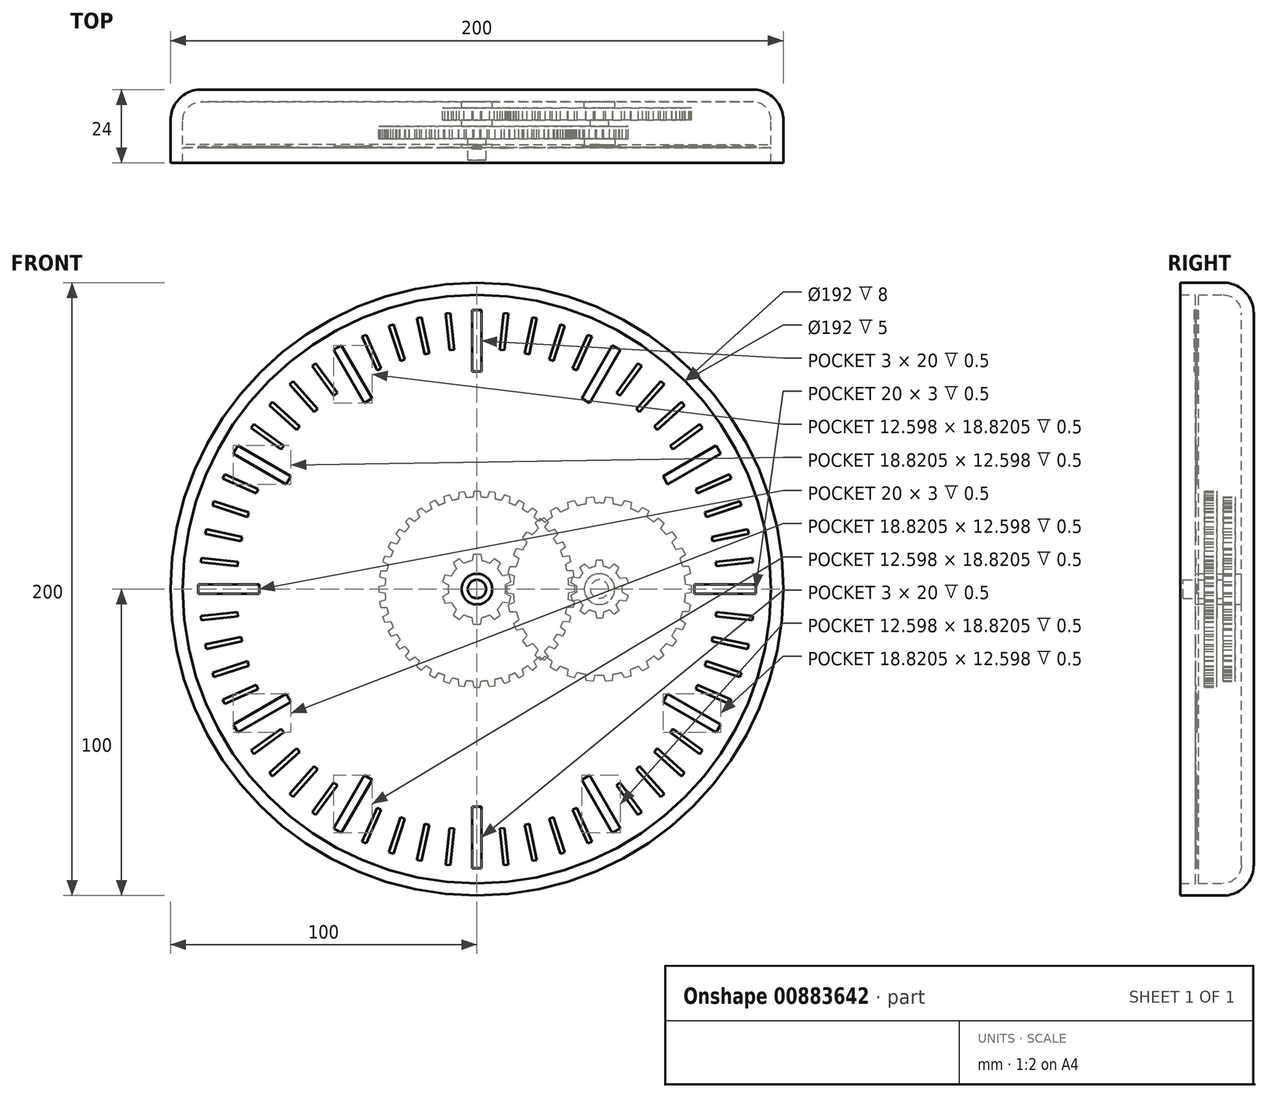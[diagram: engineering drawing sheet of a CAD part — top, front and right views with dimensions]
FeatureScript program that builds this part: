
annotation { "Feature Type Name" : "Feature", "Feature Type Description" : "" }
export const myFeature = defineFeature(function(context is Context, id is Id, definition is map)
    precondition{}
    {
        {
            var Q0;
            Q0=qCreatedBy(makeId("Front.planeOp"),FACE);
            var sketch = newSketch(context, id + "F0", { "sketchPlane" : qUnion([Q0])});
            skCircle(sketch, "E0", {"center": v(0, 0) * mm, "radius": 100 * mm});
            skSolve(sketch);
        }
        {
            var Q0;
            Q0 = qSketchRegion(id + "F0", true);
            extrude(context, id + "F1", {"entities" : qUnion([Q0]), "depth" : 24 * mm, "offsetDistance" : 25 * mm});
        }
        {
            var Q0;
            Q0=makeQuery(id+"F1.opExtrude","CAP_EDGE",EDGE,{"disambiguationData":[OSD([sQuery(id+"F0.wireOp",EDGE,"E0")])],"isStart":true});
            fillet(context, id + "F2", {"entities" : qUnion([Q0]), "radius" : 10 * mm, "tangentPropagation" : true, "allowEdgeOverflow" : false});
        }
        {
            var Q0;
            Q0=makeQuery(id+"F1.opExtrude","CAP_FACE",FACE,{"disambiguationData":[OSD([sQuery(id+"F0.wireOp",EDGE,"E0")])],"isStart":false});
            shell(context, id + "F3", {"entities" : qUnion([Q0]), "thickness" : 4 * mm});
        }
        {
            var Q0;
            {var subQ0=sQuery(id+"F0.wireOp",EDGE,"E0");Q0=makeQuery(id+"F3.opShell","OFFSET_FACE",FACE,{"disambiguationData":[OSD([subQ0]),TDD([makeQuery(id+"F1.opExtrude","CAP_FACE",FACE,{"disambiguationData":[OSD([subQ0])],"isStart":true})])]});}
            var sketch = newSketch(context, id + "F4", { "sketchPlane" : qUnion([Q0])});
            skCircle(sketch, "E1", {"center": v(0, 0) * mm, "radius": 3 * mm});
            skCircle(sketch, "E2", {"center": v(0, 0) * mm, "radius": 5 * mm});
            skCircle(sketch, "E3", {"center": v(40, 0) * mm, "radius": 3 * mm});
            skCircle(sketch, "E4", {"center": v(40, 0) * mm, "radius": 5 * mm});
            skSolve(sketch);
        }
        {
            var Q0;
            Q0 = qSketchRegion(id + "F4", true);
            extrude(context, id + "F5", {"entities" : qUnion([Q0]), "operationType" : NewBodyOperationType.ADD, "depth" : 2 * mm, "offsetDistance" : 25 * mm});
        }
        {
            var Q0;
            {var subQ0=sQuery(id+"F0.wireOp",EDGE,"E0");Q0=makeQuery(id+"F5.boolean.opBoolean","SPLIT",FACE,{"disambiguationData":[TD([makeQuery(id+"F5.opExtrude","SWEPT_FACE",FACE,{"disambiguationData":[OSD([sQuery(id+"F4.wireOp",EDGE,"E1")])]})])],"derivedFrom":makeQuery(id+"F3.opShell","OFFSET_FACE",FACE,{"disambiguationData":[OSD([subQ0]),TDD([makeQuery(id+"F1.opExtrude","CAP_FACE",FACE,{"disambiguationData":[OSD([subQ0])],"isStart":true})])]})});}
            extrude(context, id + "F6", {"entities" : qUnion([Q0]), "depth" : 19 * mm, "offsetDistance" : 25 * mm});
        }
        {
            var Q0;
            {var subQ0=sQuery(id+"F0.wireOp",EDGE,"E0");Q0=makeQuery(id+"F5.boolean.opBoolean","SPLIT",FACE,{"disambiguationData":[TD([makeQuery(id+"F5.opExtrude","SWEPT_FACE",FACE,{"disambiguationData":[OSD([sQuery(id+"F4.wireOp",EDGE,"E3")])]})])],"derivedFrom":makeQuery(id+"F3.opShell","OFFSET_FACE",FACE,{"disambiguationData":[OSD([subQ0]),TDD([makeQuery(id+"F1.opExtrude","CAP_FACE",FACE,{"disambiguationData":[OSD([subQ0])],"isStart":true})])]})});}
            extrude(context, id + "F7", {"entities" : qUnion([Q0]), "depth" : 8 * mm, "offsetDistance" : 25 * mm});
        }
        {
            var Q0;
            Q0=makeQuery(id+"F5.opExtrude","CAP_FACE",FACE,{"disambiguationData":[OSD([sQuery(id+"F4.wireOp",EDGE,"E1"),sQuery(id+"F4.wireOp",EDGE,"E2")])],"isStart":false});
            var sketch = newSketch(context, id + "F8", { "sketchPlane" : qUnion([Q0])});
            skCircle(sketch, "E5", {"center": v(0, 0) * mm, "radius": 9.38 * mm});
            skLineSegment(sketch, "E6", {"start": v(0, 11.38) * mm, "end": v(1.18, 11.38) * mm});
            skLineSegment(sketch, "E7", {"start": v(1.18, 11.38) * mm, "end": v(1.55, 9.25) * mm});
            skLineSegment(sketch, "E8.MirrorCS", {"start": v(0, 11.38) * mm, "end": v(-1.18, 11.38) * mm});
            skLineSegment(sketch, "E9.MirrorCS", {"start": v(-1.18, 11.38) * mm, "end": v(-1.55, 9.25) * mm});
            skLineSegment(sketch, "E10.1.0", {"start": v(-7.64, 8.51) * mm, "end": v(-6.7, 6.57) * mm});
            skLineSegment(sketch, "E10.1.1", {"start": v(-6.69, 9.2) * mm, "end": v(-7.64, 8.51) * mm});
            skLineSegment(sketch, "E10.1.2", {"start": v(-6.69, 9.2) * mm, "end": v(-5.73, 9.9) * mm});
            skLineSegment(sketch, "E10.1.3", {"start": v(-5.73, 9.9) * mm, "end": v(-4.18, 8.4) * mm});
            skLineSegment(sketch, "E10.2.0", {"start": v(-11.18, 2.4) * mm, "end": v(-9.27, 1.38) * mm});
            skLineSegment(sketch, "E10.2.1", {"start": v(-10.82, 3.52) * mm, "end": v(-11.18, 2.4) * mm});
            skLineSegment(sketch, "E10.2.2", {"start": v(-10.82, 3.52) * mm, "end": v(-10.45, 4.64) * mm});
            skLineSegment(sketch, "E10.2.3", {"start": v(-10.45, 4.64) * mm, "end": v(-8.31, 4.33) * mm});
            skLineSegment(sketch, "E10.3.0", {"start": v(-10.45, -4.64) * mm, "end": v(-8.31, -4.33) * mm});
            skLineSegment(sketch, "E10.3.1", {"start": v(-10.82, -3.52) * mm, "end": v(-10.45, -4.64) * mm});
            skLineSegment(sketch, "E10.3.2", {"start": v(-10.82, -3.52) * mm, "end": v(-11.18, -2.4) * mm});
            skLineSegment(sketch, "E10.3.3", {"start": v(-11.18, -2.4) * mm, "end": v(-9.27, -1.38) * mm});
            skLineSegment(sketch, "E10.4.0", {"start": v(-5.73, -9.9) * mm, "end": v(-4.18, -8.4) * mm});
            skLineSegment(sketch, "E10.4.1", {"start": v(-6.69, -9.2) * mm, "end": v(-5.73, -9.9) * mm});
            skLineSegment(sketch, "E10.4.2", {"start": v(-6.69, -9.2) * mm, "end": v(-7.64, -8.51) * mm});
            skLineSegment(sketch, "E10.4.3", {"start": v(-7.64, -8.51) * mm, "end": v(-6.7, -6.57) * mm});
            skLineSegment(sketch, "E10.5.0", {"start": v(1.18, -11.38) * mm, "end": v(1.55, -9.25) * mm});
            skLineSegment(sketch, "E10.5.1", {"start": v(0, -11.38) * mm, "end": v(1.18, -11.38) * mm});
            skLineSegment(sketch, "E10.5.2", {"start": v(0, -11.38) * mm, "end": v(-1.18, -11.38) * mm});
            skLineSegment(sketch, "E10.5.3", {"start": v(-1.18, -11.38) * mm, "end": v(-1.55, -9.25) * mm});
            skLineSegment(sketch, "E10.6.0", {"start": v(7.64, -8.51) * mm, "end": v(6.7, -6.57) * mm});
            skLineSegment(sketch, "E10.6.1", {"start": v(6.69, -9.2) * mm, "end": v(7.64, -8.51) * mm});
            skLineSegment(sketch, "E10.6.2", {"start": v(6.69, -9.2) * mm, "end": v(5.73, -9.9) * mm});
            skLineSegment(sketch, "E10.6.3", {"start": v(5.73, -9.9) * mm, "end": v(4.18, -8.4) * mm});
            skLineSegment(sketch, "E10.7.0", {"start": v(11.18, -2.4) * mm, "end": v(9.27, -1.38) * mm});
            skLineSegment(sketch, "E10.7.1", {"start": v(10.82, -3.52) * mm, "end": v(11.18, -2.4) * mm});
            skLineSegment(sketch, "E10.7.2", {"start": v(10.82, -3.52) * mm, "end": v(10.45, -4.64) * mm});
            skLineSegment(sketch, "E10.7.3", {"start": v(10.45, -4.64) * mm, "end": v(8.31, -4.33) * mm});
            skLineSegment(sketch, "E10.8.0", {"start": v(10.45, 4.64) * mm, "end": v(8.31, 4.33) * mm});
            skLineSegment(sketch, "E10.8.1", {"start": v(10.82, 3.52) * mm, "end": v(10.45, 4.64) * mm});
            skLineSegment(sketch, "E10.8.2", {"start": v(10.82, 3.52) * mm, "end": v(11.18, 2.4) * mm});
            skLineSegment(sketch, "E10.8.3", {"start": v(11.18, 2.4) * mm, "end": v(9.27, 1.38) * mm});
            skLineSegment(sketch, "E10.9.0", {"start": v(5.73, 9.9) * mm, "end": v(4.18, 8.4) * mm});
            skLineSegment(sketch, "E10.9.1", {"start": v(6.69, 9.2) * mm, "end": v(5.73, 9.9) * mm});
            skLineSegment(sketch, "E10.9.2", {"start": v(6.69, 9.2) * mm, "end": v(7.64, 8.51) * mm});
            skLineSegment(sketch, "E10.9.3", {"start": v(7.64, 8.51) * mm, "end": v(6.7, 6.57) * mm});
            skSolve(sketch);
        }
        {
            var Q0;
            Q0 = qSketchRegion(id + "F8", true);
            extrude(context, id + "F9", {"entities" : qUnion([Q0]), "operationType" : NewBodyOperationType.ADD, "depth" : 4 * mm, "offsetDistance" : 25 * mm});
        }
        {
            var Q0;
            Q0=makeQuery(id+"F5.opExtrude","CAP_FACE",FACE,{"disambiguationData":[OSD([sQuery(id+"F4.wireOp",EDGE,"E3"),sQuery(id+"F4.wireOp",EDGE,"E4")])],"isStart":false});
            var sketch = newSketch(context, id + "F10", { "sketchPlane" : qUnion([Q0])});
            skCircle(sketch, "E11", {"center": v(40, 0) * mm, "radius": 28.12 * mm});
            skLineSegment(sketch, "E12", {"start": v(9.88, 0) * mm, "end": v(9.88, 1.18) * mm});
            skLineSegment(sketch, "E13", {"start": v(9.88, 1.18) * mm, "end": v(11.92, 1.54) * mm});
            skLineSegment(sketch, "E14.MirrorCS", {"start": v(9.88, 0) * mm, "end": v(9.88, -1.18) * mm});
            skLineSegment(sketch, "E15.MirrorCS", {"start": v(9.88, -1.18) * mm, "end": v(11.92, -1.54) * mm});
            skLineSegment(sketch, "E16.1.0", {"start": v(10.29, -5.11) * mm, "end": v(12.21, -4.33) * mm});
            skLineSegment(sketch, "E16.1.1", {"start": v(10.53, -6.26) * mm, "end": v(10.29, -5.11) * mm});
            skLineSegment(sketch, "E16.1.2", {"start": v(10.53, -6.26) * mm, "end": v(10.78, -7.42) * mm});
            skLineSegment(sketch, "E16.1.3", {"start": v(10.78, -7.42) * mm, "end": v(12.85, -7.34) * mm});
            skLineSegment(sketch, "E16.2.0", {"start": v(12, -11.18) * mm, "end": v(13.72, -10.02) * mm});
            skLineSegment(sketch, "E16.2.1", {"start": v(12.48, -12.25) * mm, "end": v(12, -11.18) * mm});
            skLineSegment(sketch, "E16.2.2", {"start": v(12.48, -12.25) * mm, "end": v(12.96, -13.33) * mm});
            skLineSegment(sketch, "E16.2.3", {"start": v(12.96, -13.33) * mm, "end": v(14.97, -12.83) * mm});
            skLineSegment(sketch, "E17.1.3.0", {"start": v(14.94, -16.75) * mm, "end": v(16.38, -15.26) * mm});
            skLineSegment(sketch, "E17.3.3.0", {"start": v(15.63, -17.7) * mm, "end": v(14.94, -16.75) * mm});
            skLineSegment(sketch, "E17.6.3.0", {"start": v(15.63, -17.7) * mm, "end": v(16.32, -18.66) * mm});
            skLineSegment(sketch, "E17.9.3.0", {"start": v(16.32, -18.66) * mm, "end": v(18.18, -17.75) * mm});
            skLineSegment(sketch, "E17.1.4.0", {"start": v(18.97, -21.6) * mm, "end": v(20.07, -19.84) * mm});
            skLineSegment(sketch, "E17.3.4.0", {"start": v(19.84, -22.39) * mm, "end": v(18.97, -21.6) * mm});
            skLineSegment(sketch, "E17.6.4.0", {"start": v(19.84, -22.39) * mm, "end": v(20.72, -23.18) * mm});
            skLineSegment(sketch, "E17.9.4.0", {"start": v(20.72, -23.18) * mm, "end": v(22.35, -21.9) * mm});
            skLineSegment(sketch, "E17.1.5.0", {"start": v(23.92, -25.5) * mm, "end": v(24.63, -23.55) * mm});
            skLineSegment(sketch, "E17.3.5.0", {"start": v(24.94, -26.09) * mm, "end": v(23.92, -25.5) * mm});
            skLineSegment(sketch, "E17.6.5.0", {"start": v(24.94, -26.09) * mm, "end": v(25.96, -26.68) * mm});
            skLineSegment(sketch, "E17.9.5.0", {"start": v(25.96, -26.68) * mm, "end": v(27.3, -25.09) * mm});
            skLineSegment(sketch, "E17.1.6.0", {"start": v(29.57, -28.29) * mm, "end": v(29.86, -26.23) * mm});
            skLineSegment(sketch, "E17.3.6.0", {"start": v(30.7, -28.65) * mm, "end": v(29.57, -28.29) * mm});
            skLineSegment(sketch, "E17.6.6.0", {"start": v(30.7, -28.65) * mm, "end": v(31.81, -29.01) * mm});
            skLineSegment(sketch, "E17.9.6.0", {"start": v(31.81, -29.01) * mm, "end": v(32.78, -27.18) * mm});
            skLineSegment(sketch, "E17.1.7.0", {"start": v(35.68, -29.84) * mm, "end": v(35.53, -27.77) * mm});
            skLineSegment(sketch, "E17.3.7.0", {"start": v(36.85, -29.96) * mm, "end": v(35.68, -29.84) * mm});
            skLineSegment(sketch, "E17.6.7.0", {"start": v(36.85, -29.96) * mm, "end": v(38.02, -30.08) * mm});
            skLineSegment(sketch, "E17.9.7.0", {"start": v(38.02, -30.08) * mm, "end": v(38.6, -28.09) * mm});
            skLineSegment(sketch, "E17.1.8.0", {"start": v(41.98, -30.08) * mm, "end": v(41.4, -28.09) * mm});
            skLineSegment(sketch, "E17.3.8.0", {"start": v(43.15, -29.96) * mm, "end": v(41.98, -30.08) * mm});
            skLineSegment(sketch, "E17.6.8.0", {"start": v(43.15, -29.96) * mm, "end": v(44.32, -29.84) * mm});
            skLineSegment(sketch, "E17.9.8.0", {"start": v(44.32, -29.84) * mm, "end": v(44.47, -27.77) * mm});
            skLineSegment(sketch, "E17.1.9.0", {"start": v(48.19, -29.01) * mm, "end": v(47.22, -27.18) * mm});
            skLineSegment(sketch, "E17.3.9.0", {"start": v(49.3, -28.65) * mm, "end": v(48.19, -29.01) * mm});
            skLineSegment(sketch, "E17.6.9.0", {"start": v(49.3, -28.65) * mm, "end": v(50.43, -28.29) * mm});
            skLineSegment(sketch, "E17.9.9.0", {"start": v(50.43, -28.29) * mm, "end": v(50.14, -26.23) * mm});
            skLineSegment(sketch, "E17.1.10.0", {"start": v(54.04, -26.68) * mm, "end": v(52.7, -25.09) * mm});
            skLineSegment(sketch, "E17.3.10.0", {"start": v(55.06, -26.09) * mm, "end": v(54.04, -26.68) * mm});
            skLineSegment(sketch, "E17.6.10.0", {"start": v(55.06, -26.09) * mm, "end": v(56.08, -25.5) * mm});
            skLineSegment(sketch, "E17.9.10.0", {"start": v(56.08, -25.5) * mm, "end": v(55.37, -23.55) * mm});
            skLineSegment(sketch, "E17.1.11.0", {"start": v(59.28, -23.18) * mm, "end": v(57.65, -21.9) * mm});
            skLineSegment(sketch, "E17.3.11.0", {"start": v(60.16, -22.39) * mm, "end": v(59.28, -23.18) * mm});
            skLineSegment(sketch, "E17.6.11.0", {"start": v(60.16, -22.39) * mm, "end": v(61.03, -21.6) * mm});
            skLineSegment(sketch, "E17.9.11.0", {"start": v(61.03, -21.6) * mm, "end": v(59.93, -19.84) * mm});
            skLineSegment(sketch, "E17.1.12.0", {"start": v(63.68, -18.66) * mm, "end": v(61.82, -17.75) * mm});
            skLineSegment(sketch, "E17.3.12.0", {"start": v(64.37, -17.7) * mm, "end": v(63.68, -18.66) * mm});
            skLineSegment(sketch, "E17.6.12.0", {"start": v(64.37, -17.7) * mm, "end": v(65.06, -16.75) * mm});
            skLineSegment(sketch, "E17.9.12.0", {"start": v(65.06, -16.75) * mm, "end": v(63.62, -15.26) * mm});
            skLineSegment(sketch, "E17.1.13.0", {"start": v(67.04, -13.33) * mm, "end": v(65.03, -12.83) * mm});
            skLineSegment(sketch, "E17.3.13.0", {"start": v(67.52, -12.25) * mm, "end": v(67.04, -13.33) * mm});
            skLineSegment(sketch, "E17.6.13.0", {"start": v(67.52, -12.25) * mm, "end": v(68, -11.18) * mm});
            skLineSegment(sketch, "E17.9.13.0", {"start": v(68, -11.18) * mm, "end": v(66.28, -10.02) * mm});
            skLineSegment(sketch, "E17.1.14.0", {"start": v(69.22, -7.42) * mm, "end": v(67.15, -7.34) * mm});
            skLineSegment(sketch, "E17.3.14.0", {"start": v(69.47, -6.26) * mm, "end": v(69.22, -7.42) * mm});
            skLineSegment(sketch, "E17.6.14.0", {"start": v(69.47, -6.26) * mm, "end": v(69.71, -5.11) * mm});
            skLineSegment(sketch, "E17.9.14.0", {"start": v(69.71, -5.11) * mm, "end": v(67.79, -4.33) * mm});
            skLineSegment(sketch, "E17.1.15.0", {"start": v(70.12, -1.18) * mm, "end": v(68.08, -1.54) * mm});
            skLineSegment(sketch, "E17.3.15.0", {"start": v(70.12, 0) * mm, "end": v(70.12, -1.18) * mm});
            skLineSegment(sketch, "E17.6.15.0", {"start": v(70.12, 0) * mm, "end": v(70.12, 1.18) * mm});
            skLineSegment(sketch, "E17.9.15.0", {"start": v(70.12, 1.18) * mm, "end": v(68.08, 1.54) * mm});
            skLineSegment(sketch, "E17.1.16.0", {"start": v(69.71, 5.11) * mm, "end": v(67.79, 4.33) * mm});
            skLineSegment(sketch, "E17.3.16.0", {"start": v(69.47, 6.26) * mm, "end": v(69.71, 5.11) * mm});
            skLineSegment(sketch, "E17.6.16.0", {"start": v(69.47, 6.26) * mm, "end": v(69.22, 7.42) * mm});
            skLineSegment(sketch, "E17.9.16.0", {"start": v(69.22, 7.42) * mm, "end": v(67.15, 7.34) * mm});
            skLineSegment(sketch, "E17.1.17.0", {"start": v(68, 11.18) * mm, "end": v(66.28, 10.02) * mm});
            skLineSegment(sketch, "E17.3.17.0", {"start": v(67.52, 12.25) * mm, "end": v(68, 11.18) * mm});
            skLineSegment(sketch, "E17.6.17.0", {"start": v(67.52, 12.25) * mm, "end": v(67.04, 13.33) * mm});
            skLineSegment(sketch, "E17.9.17.0", {"start": v(67.04, 13.33) * mm, "end": v(65.03, 12.83) * mm});
            skLineSegment(sketch, "E17.1.18.0", {"start": v(65.06, 16.75) * mm, "end": v(63.62, 15.26) * mm});
            skLineSegment(sketch, "E17.3.18.0", {"start": v(64.37, 17.7) * mm, "end": v(65.06, 16.75) * mm});
            skLineSegment(sketch, "E17.6.18.0", {"start": v(64.37, 17.7) * mm, "end": v(63.68, 18.66) * mm});
            skLineSegment(sketch, "E17.9.18.0", {"start": v(63.68, 18.66) * mm, "end": v(61.82, 17.75) * mm});
            skLineSegment(sketch, "E17.1.19.0", {"start": v(61.03, 21.6) * mm, "end": v(59.93, 19.84) * mm});
            skLineSegment(sketch, "E17.3.19.0", {"start": v(60.16, 22.39) * mm, "end": v(61.03, 21.6) * mm});
            skLineSegment(sketch, "E17.6.19.0", {"start": v(60.16, 22.39) * mm, "end": v(59.28, 23.18) * mm});
            skLineSegment(sketch, "E17.9.19.0", {"start": v(59.28, 23.18) * mm, "end": v(57.65, 21.9) * mm});
            skLineSegment(sketch, "E17.1.20.0", {"start": v(56.08, 25.5) * mm, "end": v(55.37, 23.55) * mm});
            skLineSegment(sketch, "E17.3.20.0", {"start": v(55.06, 26.09) * mm, "end": v(56.08, 25.5) * mm});
            skLineSegment(sketch, "E17.6.20.0", {"start": v(55.06, 26.09) * mm, "end": v(54.04, 26.68) * mm});
            skLineSegment(sketch, "E17.9.20.0", {"start": v(54.04, 26.68) * mm, "end": v(52.7, 25.09) * mm});
            skLineSegment(sketch, "E17.1.21.0", {"start": v(50.43, 28.29) * mm, "end": v(50.14, 26.23) * mm});
            skLineSegment(sketch, "E17.3.21.0", {"start": v(49.3, 28.65) * mm, "end": v(50.43, 28.29) * mm});
            skLineSegment(sketch, "E17.6.21.0", {"start": v(49.3, 28.65) * mm, "end": v(48.19, 29.01) * mm});
            skLineSegment(sketch, "E17.9.21.0", {"start": v(48.19, 29.01) * mm, "end": v(47.22, 27.18) * mm});
            skLineSegment(sketch, "E17.1.22.0", {"start": v(44.32, 29.84) * mm, "end": v(44.47, 27.77) * mm});
            skLineSegment(sketch, "E17.3.22.0", {"start": v(43.15, 29.96) * mm, "end": v(44.32, 29.84) * mm});
            skLineSegment(sketch, "E17.6.22.0", {"start": v(43.15, 29.96) * mm, "end": v(41.98, 30.08) * mm});
            skLineSegment(sketch, "E17.9.22.0", {"start": v(41.98, 30.08) * mm, "end": v(41.4, 28.09) * mm});
            skLineSegment(sketch, "E17.1.23.0", {"start": v(38.02, 30.08) * mm, "end": v(38.6, 28.09) * mm});
            skLineSegment(sketch, "E17.3.23.0", {"start": v(36.85, 29.96) * mm, "end": v(38.02, 30.08) * mm});
            skLineSegment(sketch, "E17.6.23.0", {"start": v(36.85, 29.96) * mm, "end": v(35.68, 29.84) * mm});
            skLineSegment(sketch, "E17.9.23.0", {"start": v(35.68, 29.84) * mm, "end": v(35.53, 27.77) * mm});
            skLineSegment(sketch, "E17.1.24.0", {"start": v(31.81, 29.01) * mm, "end": v(32.78, 27.18) * mm});
            skLineSegment(sketch, "E17.3.24.0", {"start": v(30.7, 28.65) * mm, "end": v(31.81, 29.01) * mm});
            skLineSegment(sketch, "E17.6.24.0", {"start": v(30.7, 28.65) * mm, "end": v(29.57, 28.29) * mm});
            skLineSegment(sketch, "E17.9.24.0", {"start": v(29.57, 28.29) * mm, "end": v(29.86, 26.23) * mm});
            skLineSegment(sketch, "E17.1.25.0", {"start": v(25.96, 26.68) * mm, "end": v(27.3, 25.09) * mm});
            skLineSegment(sketch, "E17.3.25.0", {"start": v(24.94, 26.09) * mm, "end": v(25.96, 26.68) * mm});
            skLineSegment(sketch, "E17.6.25.0", {"start": v(24.94, 26.09) * mm, "end": v(23.92, 25.5) * mm});
            skLineSegment(sketch, "E17.9.25.0", {"start": v(23.92, 25.5) * mm, "end": v(24.63, 23.55) * mm});
            skLineSegment(sketch, "E17.1.26.0", {"start": v(20.72, 23.18) * mm, "end": v(22.35, 21.9) * mm});
            skLineSegment(sketch, "E17.3.26.0", {"start": v(19.84, 22.39) * mm, "end": v(20.72, 23.18) * mm});
            skLineSegment(sketch, "E17.6.26.0", {"start": v(19.84, 22.39) * mm, "end": v(18.97, 21.6) * mm});
            skLineSegment(sketch, "E17.9.26.0", {"start": v(18.97, 21.6) * mm, "end": v(20.07, 19.84) * mm});
            skLineSegment(sketch, "E17.1.27.0", {"start": v(16.32, 18.66) * mm, "end": v(18.18, 17.75) * mm});
            skLineSegment(sketch, "E17.3.27.0", {"start": v(15.63, 17.7) * mm, "end": v(16.32, 18.66) * mm});
            skLineSegment(sketch, "E17.6.27.0", {"start": v(15.63, 17.7) * mm, "end": v(14.94, 16.75) * mm});
            skLineSegment(sketch, "E17.9.27.0", {"start": v(14.94, 16.75) * mm, "end": v(16.38, 15.26) * mm});
            skLineSegment(sketch, "E17.1.28.0", {"start": v(12.96, 13.33) * mm, "end": v(14.97, 12.83) * mm});
            skLineSegment(sketch, "E17.3.28.0", {"start": v(12.48, 12.25) * mm, "end": v(12.96, 13.33) * mm});
            skLineSegment(sketch, "E17.6.28.0", {"start": v(12.48, 12.25) * mm, "end": v(12, 11.18) * mm});
            skLineSegment(sketch, "E17.9.28.0", {"start": v(12, 11.18) * mm, "end": v(13.72, 10.02) * mm});
            skLineSegment(sketch, "E17.1.29.0", {"start": v(10.78, 7.42) * mm, "end": v(12.85, 7.34) * mm});
            skLineSegment(sketch, "E17.3.29.0", {"start": v(10.53, 6.26) * mm, "end": v(10.78, 7.42) * mm});
            skLineSegment(sketch, "E17.6.29.0", {"start": v(10.53, 6.26) * mm, "end": v(10.29, 5.11) * mm});
            skLineSegment(sketch, "E17.9.29.0", {"start": v(10.29, 5.11) * mm, "end": v(12.21, 4.33) * mm});
            skSolve(sketch);
        }
        {
            var Q0;
            Q0 = qSketchRegion(id + "F10", true);
            extrude(context, id + "F11", {"entities" : qUnion([Q0]), "operationType" : NewBodyOperationType.ADD, "depth" : 4 * mm, "offsetDistance" : 25 * mm});
        }
        {
            var Q0;
            Q0=makeQuery(id+"F9.opExtrude","CAP_FACE",FACE,{"disambiguationData":[OSD([sQuery(id+"F8.wireOp",EDGE,"E5"),sQuery(id+"F8.wireOp",EDGE,"E6"),sQuery(id+"F8.wireOp",EDGE,"E7"),sQuery(id+"F8.wireOp",EDGE,"E8.MirrorCS"),sQuery(id+"F8.wireOp",EDGE,"E9.MirrorCS"),sQuery(id+"F8.wireOp",EDGE,"E10.1.0"),sQuery(id+"F8.wireOp",EDGE,"E10.1.1"),sQuery(id+"F8.wireOp",EDGE,"E10.1.2"),sQuery(id+"F8.wireOp",EDGE,"E10.1.3"),sQuery(id+"F8.wireOp",EDGE,"E10.2.0"),sQuery(id+"F8.wireOp",EDGE,"E10.2.1"),sQuery(id+"F8.wireOp",EDGE,"E10.2.2"),sQuery(id+"F8.wireOp",EDGE,"E10.2.3"),sQuery(id+"F8.wireOp",EDGE,"E10.3.0"),sQuery(id+"F8.wireOp",EDGE,"E10.3.1"),sQuery(id+"F8.wireOp",EDGE,"E10.3.2"),sQuery(id+"F8.wireOp",EDGE,"E10.3.3"),sQuery(id+"F8.wireOp",EDGE,"E10.4.0"),sQuery(id+"F8.wireOp",EDGE,"E10.4.1"),sQuery(id+"F8.wireOp",EDGE,"E10.4.2"),sQuery(id+"F8.wireOp",EDGE,"E10.4.3"),sQuery(id+"F8.wireOp",EDGE,"E10.5.0"),sQuery(id+"F8.wireOp",EDGE,"E10.5.1"),sQuery(id+"F8.wireOp",EDGE,"E10.5.2"),sQuery(id+"F8.wireOp",EDGE,"E10.5.3"),sQuery(id+"F8.wireOp",EDGE,"E10.6.0"),sQuery(id+"F8.wireOp",EDGE,"E10.6.1"),sQuery(id+"F8.wireOp",EDGE,"E10.6.2"),sQuery(id+"F8.wireOp",EDGE,"E10.6.3"),sQuery(id+"F8.wireOp",EDGE,"E10.7.0"),sQuery(id+"F8.wireOp",EDGE,"E10.7.1"),sQuery(id+"F8.wireOp",EDGE,"E10.7.2"),sQuery(id+"F8.wireOp",EDGE,"E10.7.3"),sQuery(id+"F8.wireOp",EDGE,"E10.8.0"),sQuery(id+"F8.wireOp",EDGE,"E10.8.1"),sQuery(id+"F8.wireOp",EDGE,"E10.8.2"),sQuery(id+"F8.wireOp",EDGE,"E10.8.3"),sQuery(id+"F8.wireOp",EDGE,"E10.9.0"),sQuery(id+"F8.wireOp",EDGE,"E10.9.1"),sQuery(id+"F8.wireOp",EDGE,"E10.9.2"),sQuery(id+"F8.wireOp",EDGE,"E10.9.3")])],"isStart":false});
            var sketch = newSketch(context, id + "F12", { "sketchPlane" : qUnion([Q0])});
            skCircle(sketch, "E18.0", {"center": v(0, 0) * mm, "radius": 3 * mm});
            skCircle(sketch, "E19.0", {"center": v(0, 0) * mm, "radius": 5 * mm});
            skSolve(sketch);
        }
        {
            var Q0;
            Q0 = qSketchRegion(id + "F12", true);
            extrude(context, id + "F13", {"entities" : qUnion([Q0]), "depth" : 2 * mm, "offsetDistance" : 25 * mm});
        }
        {
            var Q0;
            Q0=makeQuery(id+"F13.opExtrude","CAP_FACE",FACE,{"disambiguationData":[OSD([sQuery(id+"F12.wireOp",EDGE,"E18.0"),sQuery(id+"F12.wireOp",EDGE,"E19.0")])],"isStart":false});
            var sketch = newSketch(context, id + "F14", { "sketchPlane" : qUnion([Q0])});
            skCircle(sketch, "E20.0", {"center": v(0, 0) * mm, "radius": 3 * mm});
            skCircle(sketch, "E21", {"center": v(0, 0) * mm, "radius": 30 * mm});
            skLineSegment(sketch, "E22", {"start": v(0, 32) * mm, "end": v(0.94, 32) * mm});
            skLineSegment(sketch, "E23", {"start": v(0.94, 32) * mm, "end": v(1.3, 29.97) * mm});
            skLineSegment(sketch, "E24.MirrorCS", {"start": v(0, 32) * mm, "end": v(-0.94, 32) * mm});
            skLineSegment(sketch, "E25.MirrorCS", {"start": v(-0.94, 32) * mm, "end": v(-1.3, 29.97) * mm});
            skLineSegment(sketch, "E26.1.0", {"start": v(-5.94, 31.46) * mm, "end": v(-5.97, 29.4) * mm});
            skLineSegment(sketch, "E26.1.1", {"start": v(-5, 31.6) * mm, "end": v(-5.94, 31.46) * mm});
            skLineSegment(sketch, "E26.1.2", {"start": v(-5, 31.6) * mm, "end": v(-4.08, 31.75) * mm});
            skLineSegment(sketch, "E26.1.3", {"start": v(-4.08, 31.75) * mm, "end": v(-3.4, 29.8) * mm});
            skLineSegment(sketch, "E26.2.0", {"start": v(-10.78, 30.14) * mm, "end": v(-10.5, 28.1) * mm});
            skLineSegment(sketch, "E26.2.1", {"start": v(-9.89, 30.43) * mm, "end": v(-10.78, 30.14) * mm});
            skLineSegment(sketch, "E26.2.2", {"start": v(-9.89, 30.43) * mm, "end": v(-9, 30.73) * mm});
            skLineSegment(sketch, "E26.2.3", {"start": v(-9, 30.73) * mm, "end": v(-8.03, 28.9) * mm});
            skLineSegment(sketch, "E27.2.3.0", {"start": v(-15.37, 28.08) * mm, "end": v(-14.77, 26.11) * mm});
            skLineSegment(sketch, "E27.3.3.0", {"start": v(-14.53, 28.51) * mm, "end": v(-15.37, 28.08) * mm});
            skLineSegment(sketch, "E27.6.3.0", {"start": v(-14.53, 28.51) * mm, "end": v(-13.69, 28.94) * mm});
            skLineSegment(sketch, "E27.9.3.0", {"start": v(-13.69, 28.94) * mm, "end": v(-12.45, 27.3) * mm});
            skLineSegment(sketch, "E27.2.4.0", {"start": v(-19.57, 25.33) * mm, "end": v(-18.67, 23.48) * mm});
            skLineSegment(sketch, "E27.3.4.0", {"start": v(-18.8, 25.89) * mm, "end": v(-19.57, 25.33) * mm});
            skLineSegment(sketch, "E27.6.4.0", {"start": v(-18.8, 25.89) * mm, "end": v(-18.05, 26.44) * mm});
            skLineSegment(sketch, "E27.9.4.0", {"start": v(-18.05, 26.44) * mm, "end": v(-16.57, 25.01) * mm});
            skLineSegment(sketch, "E27.2.5.0", {"start": v(-23.3, 21.96) * mm, "end": v(-22.11, 20.27) * mm});
            skLineSegment(sketch, "E27.3.5.0", {"start": v(-22.63, 22.63) * mm, "end": v(-23.3, 21.96) * mm});
            skLineSegment(sketch, "E27.6.5.0", {"start": v(-22.63, 22.63) * mm, "end": v(-21.96, 23.3) * mm});
            skLineSegment(sketch, "E27.9.5.0", {"start": v(-21.96, 23.3) * mm, "end": v(-20.27, 22.11) * mm});
            skLineSegment(sketch, "E27.2.6.0", {"start": v(-26.44, 18.05) * mm, "end": v(-25.01, 16.57) * mm});
            skLineSegment(sketch, "E27.3.6.0", {"start": v(-25.89, 18.8) * mm, "end": v(-26.44, 18.05) * mm});
            skLineSegment(sketch, "E27.6.6.0", {"start": v(-25.89, 18.8) * mm, "end": v(-25.33, 19.57) * mm});
            skLineSegment(sketch, "E27.9.6.0", {"start": v(-25.33, 19.57) * mm, "end": v(-23.48, 18.67) * mm});
            skLineSegment(sketch, "E27.2.7.0", {"start": v(-28.94, 13.69) * mm, "end": v(-27.3, 12.45) * mm});
            skLineSegment(sketch, "E27.3.7.0", {"start": v(-28.51, 14.53) * mm, "end": v(-28.94, 13.69) * mm});
            skLineSegment(sketch, "E27.6.7.0", {"start": v(-28.51, 14.53) * mm, "end": v(-28.08, 15.37) * mm});
            skLineSegment(sketch, "E27.9.7.0", {"start": v(-28.08, 15.37) * mm, "end": v(-26.11, 14.77) * mm});
            skLineSegment(sketch, "E27.2.8.0", {"start": v(-30.73, 9) * mm, "end": v(-28.9, 8.03) * mm});
            skLineSegment(sketch, "E27.3.8.0", {"start": v(-30.43, 9.89) * mm, "end": v(-30.73, 9) * mm});
            skLineSegment(sketch, "E27.6.8.0", {"start": v(-30.43, 9.89) * mm, "end": v(-30.14, 10.78) * mm});
            skLineSegment(sketch, "E27.9.8.0", {"start": v(-30.14, 10.78) * mm, "end": v(-28.1, 10.5) * mm});
            skLineSegment(sketch, "E27.2.9.0", {"start": v(-31.75, 4.08) * mm, "end": v(-29.8, 3.4) * mm});
            skLineSegment(sketch, "E27.3.9.0", {"start": v(-31.6, 5) * mm, "end": v(-31.75, 4.08) * mm});
            skLineSegment(sketch, "E27.6.9.0", {"start": v(-31.6, 5) * mm, "end": v(-31.46, 5.94) * mm});
            skLineSegment(sketch, "E27.9.9.0", {"start": v(-31.46, 5.94) * mm, "end": v(-29.4, 5.97) * mm});
            skLineSegment(sketch, "E27.2.10.0", {"start": v(-32, -0.94) * mm, "end": v(-29.97, -1.3) * mm});
            skLineSegment(sketch, "E27.3.10.0", {"start": v(-32, 0) * mm, "end": v(-32, -0.94) * mm});
            skLineSegment(sketch, "E27.6.10.0", {"start": v(-32, 0) * mm, "end": v(-32, 0.94) * mm});
            skLineSegment(sketch, "E27.9.10.0", {"start": v(-32, 0.94) * mm, "end": v(-29.97, 1.3) * mm});
            skLineSegment(sketch, "E27.2.11.0", {"start": v(-31.46, -5.94) * mm, "end": v(-29.4, -5.97) * mm});
            skLineSegment(sketch, "E27.3.11.0", {"start": v(-31.6, -5) * mm, "end": v(-31.46, -5.94) * mm});
            skLineSegment(sketch, "E27.6.11.0", {"start": v(-31.6, -5) * mm, "end": v(-31.75, -4.08) * mm});
            skLineSegment(sketch, "E27.9.11.0", {"start": v(-31.75, -4.08) * mm, "end": v(-29.8, -3.4) * mm});
            skLineSegment(sketch, "E27.2.12.0", {"start": v(-30.14, -10.78) * mm, "end": v(-28.1, -10.5) * mm});
            skLineSegment(sketch, "E27.3.12.0", {"start": v(-30.43, -9.89) * mm, "end": v(-30.14, -10.78) * mm});
            skLineSegment(sketch, "E27.6.12.0", {"start": v(-30.43, -9.89) * mm, "end": v(-30.73, -9) * mm});
            skLineSegment(sketch, "E27.9.12.0", {"start": v(-30.73, -9) * mm, "end": v(-28.9, -8.03) * mm});
            skLineSegment(sketch, "E27.2.13.0", {"start": v(-28.08, -15.37) * mm, "end": v(-26.11, -14.77) * mm});
            skLineSegment(sketch, "E27.3.13.0", {"start": v(-28.51, -14.53) * mm, "end": v(-28.08, -15.37) * mm});
            skLineSegment(sketch, "E27.6.13.0", {"start": v(-28.51, -14.53) * mm, "end": v(-28.94, -13.69) * mm});
            skLineSegment(sketch, "E27.9.13.0", {"start": v(-28.94, -13.69) * mm, "end": v(-27.3, -12.45) * mm});
            skLineSegment(sketch, "E27.2.14.0", {"start": v(-25.33, -19.57) * mm, "end": v(-23.48, -18.67) * mm});
            skLineSegment(sketch, "E27.3.14.0", {"start": v(-25.89, -18.8) * mm, "end": v(-25.33, -19.57) * mm});
            skLineSegment(sketch, "E27.6.14.0", {"start": v(-25.89, -18.8) * mm, "end": v(-26.44, -18.05) * mm});
            skLineSegment(sketch, "E27.9.14.0", {"start": v(-26.44, -18.05) * mm, "end": v(-25.01, -16.57) * mm});
            skLineSegment(sketch, "E27.2.15.0", {"start": v(-21.96, -23.3) * mm, "end": v(-20.27, -22.11) * mm});
            skLineSegment(sketch, "E27.3.15.0", {"start": v(-22.63, -22.63) * mm, "end": v(-21.96, -23.3) * mm});
            skLineSegment(sketch, "E27.6.15.0", {"start": v(-22.63, -22.63) * mm, "end": v(-23.3, -21.96) * mm});
            skLineSegment(sketch, "E27.9.15.0", {"start": v(-23.3, -21.96) * mm, "end": v(-22.11, -20.27) * mm});
            skLineSegment(sketch, "E27.2.16.0", {"start": v(-18.05, -26.44) * mm, "end": v(-16.57, -25.01) * mm});
            skLineSegment(sketch, "E27.3.16.0", {"start": v(-18.8, -25.89) * mm, "end": v(-18.05, -26.44) * mm});
            skLineSegment(sketch, "E27.6.16.0", {"start": v(-18.8, -25.89) * mm, "end": v(-19.57, -25.33) * mm});
            skLineSegment(sketch, "E27.9.16.0", {"start": v(-19.57, -25.33) * mm, "end": v(-18.67, -23.48) * mm});
            skLineSegment(sketch, "E27.2.17.0", {"start": v(-13.69, -28.94) * mm, "end": v(-12.45, -27.3) * mm});
            skLineSegment(sketch, "E27.3.17.0", {"start": v(-14.53, -28.51) * mm, "end": v(-13.69, -28.94) * mm});
            skLineSegment(sketch, "E27.6.17.0", {"start": v(-14.53, -28.51) * mm, "end": v(-15.37, -28.08) * mm});
            skLineSegment(sketch, "E27.9.17.0", {"start": v(-15.37, -28.08) * mm, "end": v(-14.77, -26.11) * mm});
            skLineSegment(sketch, "E27.2.18.0", {"start": v(-9, -30.73) * mm, "end": v(-8.03, -28.9) * mm});
            skLineSegment(sketch, "E27.3.18.0", {"start": v(-9.89, -30.43) * mm, "end": v(-9, -30.73) * mm});
            skLineSegment(sketch, "E27.6.18.0", {"start": v(-9.89, -30.43) * mm, "end": v(-10.78, -30.14) * mm});
            skLineSegment(sketch, "E27.9.18.0", {"start": v(-10.78, -30.14) * mm, "end": v(-10.5, -28.1) * mm});
            skLineSegment(sketch, "E27.2.19.0", {"start": v(-4.08, -31.75) * mm, "end": v(-3.4, -29.8) * mm});
            skLineSegment(sketch, "E27.3.19.0", {"start": v(-5, -31.6) * mm, "end": v(-4.08, -31.75) * mm});
            skLineSegment(sketch, "E27.6.19.0", {"start": v(-5, -31.6) * mm, "end": v(-5.94, -31.46) * mm});
            skLineSegment(sketch, "E27.9.19.0", {"start": v(-5.94, -31.46) * mm, "end": v(-5.97, -29.4) * mm});
            skLineSegment(sketch, "E27.2.20.0", {"start": v(0.94, -32) * mm, "end": v(1.3, -29.97) * mm});
            skLineSegment(sketch, "E27.3.20.0", {"start": v(0, -32) * mm, "end": v(0.94, -32) * mm});
            skLineSegment(sketch, "E27.6.20.0", {"start": v(0, -32) * mm, "end": v(-0.94, -32) * mm});
            skLineSegment(sketch, "E27.9.20.0", {"start": v(-0.94, -32) * mm, "end": v(-1.3, -29.97) * mm});
            skLineSegment(sketch, "E27.2.21.0", {"start": v(5.94, -31.46) * mm, "end": v(5.97, -29.4) * mm});
            skLineSegment(sketch, "E27.3.21.0", {"start": v(5, -31.6) * mm, "end": v(5.94, -31.46) * mm});
            skLineSegment(sketch, "E27.6.21.0", {"start": v(5, -31.6) * mm, "end": v(4.08, -31.75) * mm});
            skLineSegment(sketch, "E27.9.21.0", {"start": v(4.08, -31.75) * mm, "end": v(3.4, -29.8) * mm});
            skLineSegment(sketch, "E27.2.22.0", {"start": v(10.78, -30.14) * mm, "end": v(10.5, -28.1) * mm});
            skLineSegment(sketch, "E27.3.22.0", {"start": v(9.89, -30.43) * mm, "end": v(10.78, -30.14) * mm});
            skLineSegment(sketch, "E27.6.22.0", {"start": v(9.89, -30.43) * mm, "end": v(9, -30.73) * mm});
            skLineSegment(sketch, "E27.9.22.0", {"start": v(9, -30.73) * mm, "end": v(8.03, -28.9) * mm});
            skLineSegment(sketch, "E27.2.23.0", {"start": v(15.37, -28.08) * mm, "end": v(14.77, -26.11) * mm});
            skLineSegment(sketch, "E27.3.23.0", {"start": v(14.53, -28.51) * mm, "end": v(15.37, -28.08) * mm});
            skLineSegment(sketch, "E27.6.23.0", {"start": v(14.53, -28.51) * mm, "end": v(13.69, -28.94) * mm});
            skLineSegment(sketch, "E27.9.23.0", {"start": v(13.69, -28.94) * mm, "end": v(12.45, -27.3) * mm});
            skLineSegment(sketch, "E27.2.24.0", {"start": v(19.57, -25.33) * mm, "end": v(18.67, -23.48) * mm});
            skLineSegment(sketch, "E27.3.24.0", {"start": v(18.8, -25.89) * mm, "end": v(19.57, -25.33) * mm});
            skLineSegment(sketch, "E27.6.24.0", {"start": v(18.8, -25.89) * mm, "end": v(18.05, -26.44) * mm});
            skLineSegment(sketch, "E27.9.24.0", {"start": v(18.05, -26.44) * mm, "end": v(16.57, -25.01) * mm});
            skLineSegment(sketch, "E27.2.25.0", {"start": v(23.3, -21.96) * mm, "end": v(22.11, -20.27) * mm});
            skLineSegment(sketch, "E27.3.25.0", {"start": v(22.63, -22.63) * mm, "end": v(23.3, -21.96) * mm});
            skLineSegment(sketch, "E27.6.25.0", {"start": v(22.63, -22.63) * mm, "end": v(21.96, -23.3) * mm});
            skLineSegment(sketch, "E27.9.25.0", {"start": v(21.96, -23.3) * mm, "end": v(20.27, -22.11) * mm});
            skLineSegment(sketch, "E27.2.26.0", {"start": v(26.44, -18.05) * mm, "end": v(25.01, -16.57) * mm});
            skLineSegment(sketch, "E27.3.26.0", {"start": v(25.89, -18.8) * mm, "end": v(26.44, -18.05) * mm});
            skLineSegment(sketch, "E27.6.26.0", {"start": v(25.89, -18.8) * mm, "end": v(25.33, -19.57) * mm});
            skLineSegment(sketch, "E27.9.26.0", {"start": v(25.33, -19.57) * mm, "end": v(23.48, -18.67) * mm});
            skLineSegment(sketch, "E27.2.27.0", {"start": v(28.94, -13.69) * mm, "end": v(27.3, -12.45) * mm});
            skLineSegment(sketch, "E27.3.27.0", {"start": v(28.51, -14.53) * mm, "end": v(28.94, -13.69) * mm});
            skLineSegment(sketch, "E27.6.27.0", {"start": v(28.51, -14.53) * mm, "end": v(28.08, -15.37) * mm});
            skLineSegment(sketch, "E27.9.27.0", {"start": v(28.08, -15.37) * mm, "end": v(26.11, -14.77) * mm});
            skLineSegment(sketch, "E27.2.28.0", {"start": v(30.73, -9) * mm, "end": v(28.9, -8.03) * mm});
            skLineSegment(sketch, "E27.3.28.0", {"start": v(30.43, -9.89) * mm, "end": v(30.73, -9) * mm});
            skLineSegment(sketch, "E27.6.28.0", {"start": v(30.43, -9.89) * mm, "end": v(30.14, -10.78) * mm});
            skLineSegment(sketch, "E27.9.28.0", {"start": v(30.14, -10.78) * mm, "end": v(28.1, -10.5) * mm});
            skLineSegment(sketch, "E27.2.29.0", {"start": v(31.75, -4.08) * mm, "end": v(29.8, -3.4) * mm});
            skLineSegment(sketch, "E27.3.29.0", {"start": v(31.6, -5) * mm, "end": v(31.75, -4.08) * mm});
            skLineSegment(sketch, "E27.6.29.0", {"start": v(31.6, -5) * mm, "end": v(31.46, -5.94) * mm});
            skLineSegment(sketch, "E27.9.29.0", {"start": v(31.46, -5.94) * mm, "end": v(29.4, -5.97) * mm});
            skLineSegment(sketch, "E27.2.30.0", {"start": v(32, 0.94) * mm, "end": v(29.97, 1.3) * mm});
            skLineSegment(sketch, "E27.3.30.0", {"start": v(32, 0) * mm, "end": v(32, 0.94) * mm});
            skLineSegment(sketch, "E27.6.30.0", {"start": v(32, 0) * mm, "end": v(32, -0.94) * mm});
            skLineSegment(sketch, "E27.9.30.0", {"start": v(32, -0.94) * mm, "end": v(29.97, -1.3) * mm});
            skLineSegment(sketch, "E27.2.31.0", {"start": v(31.46, 5.94) * mm, "end": v(29.4, 5.97) * mm});
            skLineSegment(sketch, "E27.3.31.0", {"start": v(31.6, 5) * mm, "end": v(31.46, 5.94) * mm});
            skLineSegment(sketch, "E27.6.31.0", {"start": v(31.6, 5) * mm, "end": v(31.75, 4.08) * mm});
            skLineSegment(sketch, "E27.9.31.0", {"start": v(31.75, 4.08) * mm, "end": v(29.8, 3.4) * mm});
            skLineSegment(sketch, "E27.2.32.0", {"start": v(30.14, 10.78) * mm, "end": v(28.1, 10.5) * mm});
            skLineSegment(sketch, "E27.3.32.0", {"start": v(30.43, 9.89) * mm, "end": v(30.14, 10.78) * mm});
            skLineSegment(sketch, "E27.6.32.0", {"start": v(30.43, 9.89) * mm, "end": v(30.73, 9) * mm});
            skLineSegment(sketch, "E27.9.32.0", {"start": v(30.73, 9) * mm, "end": v(28.9, 8.03) * mm});
            skLineSegment(sketch, "E27.2.33.0", {"start": v(28.08, 15.37) * mm, "end": v(26.11, 14.77) * mm});
            skLineSegment(sketch, "E27.3.33.0", {"start": v(28.51, 14.53) * mm, "end": v(28.08, 15.37) * mm});
            skLineSegment(sketch, "E27.6.33.0", {"start": v(28.51, 14.53) * mm, "end": v(28.94, 13.69) * mm});
            skLineSegment(sketch, "E27.9.33.0", {"start": v(28.94, 13.69) * mm, "end": v(27.3, 12.45) * mm});
            skLineSegment(sketch, "E27.2.34.0", {"start": v(25.33, 19.57) * mm, "end": v(23.48, 18.67) * mm});
            skLineSegment(sketch, "E27.3.34.0", {"start": v(25.89, 18.8) * mm, "end": v(25.33, 19.57) * mm});
            skLineSegment(sketch, "E27.6.34.0", {"start": v(25.89, 18.8) * mm, "end": v(26.44, 18.05) * mm});
            skLineSegment(sketch, "E27.9.34.0", {"start": v(26.44, 18.05) * mm, "end": v(25.01, 16.57) * mm});
            skLineSegment(sketch, "E27.2.35.0", {"start": v(21.96, 23.3) * mm, "end": v(20.27, 22.11) * mm});
            skLineSegment(sketch, "E27.3.35.0", {"start": v(22.63, 22.63) * mm, "end": v(21.96, 23.3) * mm});
            skLineSegment(sketch, "E27.6.35.0", {"start": v(22.63, 22.63) * mm, "end": v(23.3, 21.96) * mm});
            skLineSegment(sketch, "E27.9.35.0", {"start": v(23.3, 21.96) * mm, "end": v(22.11, 20.27) * mm});
            skLineSegment(sketch, "E27.2.36.0", {"start": v(18.05, 26.44) * mm, "end": v(16.57, 25.01) * mm});
            skLineSegment(sketch, "E27.3.36.0", {"start": v(18.8, 25.89) * mm, "end": v(18.05, 26.44) * mm});
            skLineSegment(sketch, "E27.6.36.0", {"start": v(18.8, 25.89) * mm, "end": v(19.57, 25.33) * mm});
            skLineSegment(sketch, "E27.9.36.0", {"start": v(19.57, 25.33) * mm, "end": v(18.67, 23.48) * mm});
            skLineSegment(sketch, "E27.2.37.0", {"start": v(13.69, 28.94) * mm, "end": v(12.45, 27.3) * mm});
            skLineSegment(sketch, "E27.3.37.0", {"start": v(14.53, 28.51) * mm, "end": v(13.69, 28.94) * mm});
            skLineSegment(sketch, "E27.6.37.0", {"start": v(14.53, 28.51) * mm, "end": v(15.37, 28.08) * mm});
            skLineSegment(sketch, "E27.9.37.0", {"start": v(15.37, 28.08) * mm, "end": v(14.77, 26.11) * mm});
            skLineSegment(sketch, "E27.2.38.0", {"start": v(9, 30.73) * mm, "end": v(8.03, 28.9) * mm});
            skLineSegment(sketch, "E27.3.38.0", {"start": v(9.89, 30.43) * mm, "end": v(9, 30.73) * mm});
            skLineSegment(sketch, "E27.6.38.0", {"start": v(9.89, 30.43) * mm, "end": v(10.78, 30.14) * mm});
            skLineSegment(sketch, "E27.9.38.0", {"start": v(10.78, 30.14) * mm, "end": v(10.5, 28.1) * mm});
            skLineSegment(sketch, "E27.2.39.0", {"start": v(4.08, 31.75) * mm, "end": v(3.4, 29.8) * mm});
            skLineSegment(sketch, "E27.3.39.0", {"start": v(5, 31.6) * mm, "end": v(4.08, 31.75) * mm});
            skLineSegment(sketch, "E27.6.39.0", {"start": v(5, 31.6) * mm, "end": v(5.94, 31.46) * mm});
            skLineSegment(sketch, "E27.9.39.0", {"start": v(5.94, 31.46) * mm, "end": v(5.97, 29.4) * mm});
            skSolve(sketch);
        }
        {
            var Q0;
            Q0 = qSketchRegion(id + "F14", true);
            extrude(context, id + "F15", {"entities" : qUnion([Q0]), "operationType" : NewBodyOperationType.ADD, "depth" : 4 * mm, "offsetDistance" : 25 * mm});
        }
        {
            var Q0;
            Q0=makeQuery(id+"F7.opExtrude","CAP_FACE",FACE,{"disambiguationData":[OSD([sQuery(id+"F0.wireOp",EDGE,"E0")])],"isStart":false});
            var sketch = newSketch(context, id + "F16", { "sketchPlane" : qUnion([Q0])});
            skCircle(sketch, "E28", {"center": v(40, 0) * mm, "radius": 7.5 * mm});
            skLineSegment(sketch, "E29", {"start": v(40, 0) * mm, "end": v(40, 7.5) * mm, "construction": true});
            skLineSegment(sketch, "E30", {"start": v(38.68, 7.38) * mm, "end": v(39.06, 9.5) * mm});
            skLineSegment(sketch, "E31", {"start": v(39.06, 9.5) * mm, "end": v(40.94, 9.5) * mm});
            skLineSegment(sketch, "E32.MirrorCS", {"start": v(41.32, 7.38) * mm, "end": v(40.94, 9.5) * mm});
            skLineSegment(sketch, "E33.1.0", {"start": v(34.6, 5.2) * mm, "end": v(33.65, 7.13) * mm});
            skLineSegment(sketch, "E33.1.1", {"start": v(33.65, 7.13) * mm, "end": v(35.18, 8.24) * mm});
            skLineSegment(sketch, "E33.1.2", {"start": v(36.72, 6.75) * mm, "end": v(35.18, 8.24) * mm});
            skLineSegment(sketch, "E33.2.0", {"start": v(32.57, 1.03) * mm, "end": v(30.67, 2.04) * mm});
            skLineSegment(sketch, "E33.2.1", {"start": v(30.67, 2.04) * mm, "end": v(31.26, 3.83) * mm});
            skLineSegment(sketch, "E33.2.2", {"start": v(33.38, 3.53) * mm, "end": v(31.26, 3.83) * mm});
            skLineSegment(sketch, "E34.1.3.0", {"start": v(33.38, -3.53) * mm, "end": v(31.26, -3.83) * mm});
            skLineSegment(sketch, "E34.3.3.0", {"start": v(31.26, -3.83) * mm, "end": v(30.67, -2.04) * mm});
            skLineSegment(sketch, "E34.6.3.0", {"start": v(32.57, -1.03) * mm, "end": v(30.67, -2.04) * mm});
            skLineSegment(sketch, "E34.1.4.0", {"start": v(36.72, -6.75) * mm, "end": v(35.18, -8.24) * mm});
            skLineSegment(sketch, "E34.3.4.0", {"start": v(35.18, -8.24) * mm, "end": v(33.65, -7.13) * mm});
            skLineSegment(sketch, "E34.6.4.0", {"start": v(34.6, -5.2) * mm, "end": v(33.65, -7.13) * mm});
            skLineSegment(sketch, "E34.1.5.0", {"start": v(41.32, -7.38) * mm, "end": v(40.94, -9.5) * mm});
            skLineSegment(sketch, "E34.3.5.0", {"start": v(40.94, -9.5) * mm, "end": v(39.06, -9.5) * mm});
            skLineSegment(sketch, "E34.6.5.0", {"start": v(38.68, -7.38) * mm, "end": v(39.06, -9.5) * mm});
            skLineSegment(sketch, "E34.1.6.0", {"start": v(45.4, -5.2) * mm, "end": v(46.35, -7.13) * mm});
            skLineSegment(sketch, "E34.3.6.0", {"start": v(46.35, -7.13) * mm, "end": v(44.82, -8.24) * mm});
            skLineSegment(sketch, "E34.6.6.0", {"start": v(43.28, -6.75) * mm, "end": v(44.82, -8.24) * mm});
            skLineSegment(sketch, "E34.1.7.0", {"start": v(47.43, -1.03) * mm, "end": v(49.33, -2.04) * mm});
            skLineSegment(sketch, "E34.3.7.0", {"start": v(49.33, -2.04) * mm, "end": v(48.74, -3.83) * mm});
            skLineSegment(sketch, "E34.6.7.0", {"start": v(46.62, -3.53) * mm, "end": v(48.74, -3.83) * mm});
            skLineSegment(sketch, "E34.1.8.0", {"start": v(46.62, 3.53) * mm, "end": v(48.74, 3.83) * mm});
            skLineSegment(sketch, "E34.3.8.0", {"start": v(48.74, 3.83) * mm, "end": v(49.33, 2.04) * mm});
            skLineSegment(sketch, "E34.6.8.0", {"start": v(47.43, 1.03) * mm, "end": v(49.33, 2.04) * mm});
            skLineSegment(sketch, "E34.1.9.0", {"start": v(43.28, 6.75) * mm, "end": v(44.82, 8.24) * mm});
            skLineSegment(sketch, "E34.3.9.0", {"start": v(44.82, 8.24) * mm, "end": v(46.35, 7.13) * mm});
            skLineSegment(sketch, "E34.6.9.0", {"start": v(45.4, 5.2) * mm, "end": v(46.35, 7.13) * mm});
            skSolve(sketch);
        }
        {
            var Q0;
            Q0 = qSketchRegion(id + "F16", true);
            extrude(context, id + "F17", {"entities" : qUnion([Q0]), "operationType" : NewBodyOperationType.ADD, "depth" : 4 * mm, "offsetDistance" : 25 * mm});
        }
        {
            var Q0;
            Q0=makeQuery(id+"F17.opExtrude","CAP_FACE",FACE,{"disambiguationData":[OSD([sQuery(id+"F16.wireOp",EDGE,"E28"),sQuery(id+"F16.wireOp",EDGE,"E30"),sQuery(id+"F16.wireOp",EDGE,"E31"),sQuery(id+"F16.wireOp",EDGE,"E32.MirrorCS"),sQuery(id+"F16.wireOp",EDGE,"E33.1.0"),sQuery(id+"F16.wireOp",EDGE,"E33.1.1"),sQuery(id+"F16.wireOp",EDGE,"E33.1.2"),sQuery(id+"F16.wireOp",EDGE,"E33.2.0"),sQuery(id+"F16.wireOp",EDGE,"E33.2.1"),sQuery(id+"F16.wireOp",EDGE,"E33.2.2"),sQuery(id+"F16.wireOp",EDGE,"E34.1.3.0"),sQuery(id+"F16.wireOp",EDGE,"E34.3.3.0"),sQuery(id+"F16.wireOp",EDGE,"E34.6.3.0"),sQuery(id+"F16.wireOp",EDGE,"E34.1.4.0"),sQuery(id+"F16.wireOp",EDGE,"E34.3.4.0"),sQuery(id+"F16.wireOp",EDGE,"E34.6.4.0"),sQuery(id+"F16.wireOp",EDGE,"E34.1.5.0"),sQuery(id+"F16.wireOp",EDGE,"E34.3.5.0"),sQuery(id+"F16.wireOp",EDGE,"E34.6.5.0"),sQuery(id+"F16.wireOp",EDGE,"E34.1.6.0"),sQuery(id+"F16.wireOp",EDGE,"E34.3.6.0"),sQuery(id+"F16.wireOp",EDGE,"E34.6.6.0"),sQuery(id+"F16.wireOp",EDGE,"E34.1.7.0"),sQuery(id+"F16.wireOp",EDGE,"E34.3.7.0"),sQuery(id+"F16.wireOp",EDGE,"E34.6.7.0"),sQuery(id+"F16.wireOp",EDGE,"E34.1.8.0"),sQuery(id+"F16.wireOp",EDGE,"E34.3.8.0"),sQuery(id+"F16.wireOp",EDGE,"E34.6.8.0"),sQuery(id+"F16.wireOp",EDGE,"E34.1.9.0"),sQuery(id+"F16.wireOp",EDGE,"E34.3.9.0"),sQuery(id+"F16.wireOp",EDGE,"E34.6.9.0")])],"isStart":false});
            var sketch = newSketch(context, id + "F18", { "sketchPlane" : qUnion([Q0])});
            skCircle(sketch, "E35.0", {"center": v(40, 0) * mm, "radius": 3 * mm});
            skSolve(sketch);
        }
        {
            var Q0;
            Q0 = qSketchRegion(id + "F18", true);
            extrude(context, id + "F19", {"entities" : qUnion([Q0]), "operationType" : NewBodyOperationType.ADD, "depth" : 2 * mm, "offsetDistance" : 25 * mm});
        }
        {
            var Q0;
            Q0=makeQuery(id+"F19.opExtrude","CAP_FACE",FACE,{"disambiguationData":[OSD([sQuery(id+"F18.wireOp",EDGE,"E35.0")])],"isStart":false});
            var sketch = newSketch(context, id + "F20", { "sketchPlane" : qUnion([Q0])});
            skCircle(sketch, "E36", {"center": v(0, 0) * mm, "radius": 98 * mm});
            skCircle(sketch, "E37.0", {"center": v(0, 0) * mm, "radius": 5 * mm});
            skSolve(sketch);
        }
        {
            var Q0;
            Q0 = qSketchRegion(id + "F20", true);
            extrude(context, id + "F21", {"entities" : qUnion([Q0]), "depth" : 1 * mm, "offsetDistance" : 25 * mm});
        }
        {
            var Q0;
            Q0=makeQuery(id+"F21.opExtrude","SWEPT_BODY",BODY,{"disambiguationData":[OSD([sQuery(id+"F20.wireOp",EDGE,"E36"),sQuery(id+"F20.wireOp",EDGE,"E37.0")])]});
            var Q1;
            Q1=makeQuery(id+"F1.opExtrude","SWEPT_BODY",BODY,{"disambiguationData":[OSD([sQuery(id+"F0.wireOp",EDGE,"E0")])]});
            booleanBodies(context, id + "F22", {"operationType" : BooleanOperationType.SUBTRACTION, "tools" : qUnion([Q0]), "targets" : qUnion([Q1]), "keepTools" : true});
        }
        {
            var Q0;
            Q0=makeQuery(id+"F21.opExtrude","CAP_FACE",FACE,{"disambiguationData":[OSD([sQuery(id+"F20.wireOp",EDGE,"E36"),sQuery(id+"F20.wireOp",EDGE,"E37.0")])],"isStart":true});
            var sketch = newSketch(context, id + "F23", { "sketchPlane" : qUnion([Q0])});
            skCircle(sketch, "E38.0", {"center": v(-40, 0) * mm, "radius": 3 * mm});
            skCircle(sketch, "E39", {"center": v(-40, 0) * mm, "radius": 5 * mm});
            skSolve(sketch);
        }
        {
            var Q0;
            Q0 = qSketchRegion(id + "F23", true);
            extrude(context, id + "F24", {"entities" : qUnion([Q0]), "operationType" : NewBodyOperationType.ADD, "endBound" : BoundingType.UP_TO_NEXT, "depth" : 25 * mm, "offsetDistance" : 25 * mm});
        }
        {
            var Q0;
            Q0=makeQuery(id+"F21.opExtrude","CAP_FACE",FACE,{"disambiguationData":[OSD([sQuery(id+"F20.wireOp",EDGE,"E36"),sQuery(id+"F20.wireOp",EDGE,"E37.0")])],"isStart":false});
            var sketch = newSketch(context, id + "F25", { "sketchPlane" : qUnion([Q0])});
            skLineSegment(sketch, "E40.bottom", {"start": v(1.5, 91) * mm, "end": v(-1.5, 91) * mm});
            skLineSegment(sketch, "E40.top", {"start": v(1.5, 71) * mm, "end": v(-1.5, 71) * mm});
            skLineSegment(sketch, "E40.left", {"start": v(1.5, 91) * mm, "end": v(1.5, 71) * mm});
            skLineSegment(sketch, "E40.right", {"start": v(-1.5, 91) * mm, "end": v(-1.5, 71) * mm});
            skPoint(sketch, "E40.middle", {"position": v(0, 81) * mm});
            skLineSegment(sketch, "E41.1.0", {"start": v(-44.2, 79.56) * mm, "end": v(-34.2, 62.24) * mm});
            skLineSegment(sketch, "E41.1.1", {"start": v(-46.8, 78.06) * mm, "end": v(-36.8, 60.74) * mm});
            skLineSegment(sketch, "E41.1.2", {"start": v(-44.2, 79.56) * mm, "end": v(-46.8, 78.06) * mm});
            skLineSegment(sketch, "E41.1.3", {"start": v(-34.2, 62.24) * mm, "end": v(-36.8, 60.74) * mm});
            skLineSegment(sketch, "E41.2.0", {"start": v(-78.06, 46.8) * mm, "end": v(-60.74, 36.8) * mm});
            skLineSegment(sketch, "E41.2.1", {"start": v(-79.56, 44.2) * mm, "end": v(-62.24, 34.2) * mm});
            skLineSegment(sketch, "E41.2.2", {"start": v(-78.06, 46.8) * mm, "end": v(-79.56, 44.2) * mm});
            skLineSegment(sketch, "E41.2.3", {"start": v(-60.74, 36.8) * mm, "end": v(-62.24, 34.2) * mm});
            skLineSegment(sketch, "E41.3.0", {"start": v(-91, 1.5) * mm, "end": v(-71, 1.5) * mm});
            skLineSegment(sketch, "E41.3.1", {"start": v(-91, -1.5) * mm, "end": v(-71, -1.5) * mm});
            skLineSegment(sketch, "E41.3.2", {"start": v(-91, 1.5) * mm, "end": v(-91, -1.5) * mm});
            skLineSegment(sketch, "E41.3.3", {"start": v(-71, 1.5) * mm, "end": v(-71, -1.5) * mm});
            skLineSegment(sketch, "E41.4.0", {"start": v(-79.56, -44.2) * mm, "end": v(-62.24, -34.2) * mm});
            skLineSegment(sketch, "E41.4.1", {"start": v(-78.06, -46.8) * mm, "end": v(-60.74, -36.8) * mm});
            skLineSegment(sketch, "E41.4.2", {"start": v(-79.56, -44.2) * mm, "end": v(-78.06, -46.8) * mm});
            skLineSegment(sketch, "E41.4.3", {"start": v(-62.24, -34.2) * mm, "end": v(-60.74, -36.8) * mm});
            skLineSegment(sketch, "E41.5.0", {"start": v(-46.8, -78.06) * mm, "end": v(-36.8, -60.74) * mm});
            skLineSegment(sketch, "E41.5.1", {"start": v(-44.2, -79.56) * mm, "end": v(-34.2, -62.24) * mm});
            skLineSegment(sketch, "E41.5.2", {"start": v(-46.8, -78.06) * mm, "end": v(-44.2, -79.56) * mm});
            skLineSegment(sketch, "E41.5.3", {"start": v(-36.8, -60.74) * mm, "end": v(-34.2, -62.24) * mm});
            skLineSegment(sketch, "E41.6.0", {"start": v(-1.5, -91) * mm, "end": v(-1.5, -71) * mm});
            skLineSegment(sketch, "E41.6.1", {"start": v(1.5, -91) * mm, "end": v(1.5, -71) * mm});
            skLineSegment(sketch, "E41.6.2", {"start": v(-1.5, -91) * mm, "end": v(1.5, -91) * mm});
            skLineSegment(sketch, "E41.6.3", {"start": v(-1.5, -71) * mm, "end": v(1.5, -71) * mm});
            skLineSegment(sketch, "E41.7.0", {"start": v(44.2, -79.56) * mm, "end": v(34.2, -62.24) * mm});
            skLineSegment(sketch, "E41.7.1", {"start": v(46.8, -78.06) * mm, "end": v(36.8, -60.74) * mm});
            skLineSegment(sketch, "E41.7.2", {"start": v(44.2, -79.56) * mm, "end": v(46.8, -78.06) * mm});
            skLineSegment(sketch, "E41.7.3", {"start": v(34.2, -62.24) * mm, "end": v(36.8, -60.74) * mm});
            skLineSegment(sketch, "E41.8.0", {"start": v(78.06, -46.8) * mm, "end": v(60.74, -36.8) * mm});
            skLineSegment(sketch, "E41.8.1", {"start": v(79.56, -44.2) * mm, "end": v(62.24, -34.2) * mm});
            skLineSegment(sketch, "E41.8.2", {"start": v(78.06, -46.8) * mm, "end": v(79.56, -44.2) * mm});
            skLineSegment(sketch, "E41.8.3", {"start": v(60.74, -36.8) * mm, "end": v(62.24, -34.2) * mm});
            skLineSegment(sketch, "E41.9.0", {"start": v(91, -1.5) * mm, "end": v(71, -1.5) * mm});
            skLineSegment(sketch, "E41.9.1", {"start": v(91, 1.5) * mm, "end": v(71, 1.5) * mm});
            skLineSegment(sketch, "E41.9.2", {"start": v(91, -1.5) * mm, "end": v(91, 1.5) * mm});
            skLineSegment(sketch, "E41.9.3", {"start": v(71, -1.5) * mm, "end": v(71, 1.5) * mm});
            skLineSegment(sketch, "E41.10.0", {"start": v(79.56, 44.2) * mm, "end": v(62.24, 34.2) * mm});
            skLineSegment(sketch, "E41.10.1", {"start": v(78.06, 46.8) * mm, "end": v(60.74, 36.8) * mm});
            skLineSegment(sketch, "E41.10.2", {"start": v(79.56, 44.2) * mm, "end": v(78.06, 46.8) * mm});
            skLineSegment(sketch, "E41.10.3", {"start": v(62.24, 34.2) * mm, "end": v(60.74, 36.8) * mm});
            skLineSegment(sketch, "E41.11.0", {"start": v(46.8, 78.06) * mm, "end": v(36.8, 60.74) * mm});
            skLineSegment(sketch, "E41.11.1", {"start": v(44.2, 79.56) * mm, "end": v(34.2, 62.24) * mm});
            skLineSegment(sketch, "E41.11.2", {"start": v(46.8, 78.06) * mm, "end": v(44.2, 79.56) * mm});
            skLineSegment(sketch, "E41.11.3", {"start": v(36.8, 60.74) * mm, "end": v(34.2, 62.24) * mm});
            skPoint(sketch, "E41.center", {"position": v(0, 0) * mm});
            skSolve(sketch);
        }
        {
            var Q0;
            Q0 = qSketchRegion(id + "F25", true);
            extrude(context, id + "F26", {"entities" : qUnion([Q0]), "operationType" : NewBodyOperationType.REMOVE, "oppositeDirection" : true, "depth" : 0.5 * mm, "offsetDistance" : 25 * mm});
        }
        {
            var Q0;
            Q0=makeQuery(id+"F21.opExtrude","CAP_FACE",FACE,{"disambiguationData":[OSD([sQuery(id+"F20.wireOp",EDGE,"E36"),sQuery(id+"F20.wireOp",EDGE,"E37.0")])],"isStart":false});
            var sketch = newSketch(context, id + "F27", { "sketchPlane" : qUnion([Q0])});
            skLineSegment(sketch, "E42.bottom", {"start": v(0.75, 90.5) * mm, "end": v(-0.75, 90.5) * mm});
            skLineSegment(sketch, "E42.top", {"start": v(0.75, 78.5) * mm, "end": v(-0.75, 78.5) * mm});
            skLineSegment(sketch, "E42.left", {"start": v(0.75, 90.5) * mm, "end": v(0.75, 78.5) * mm});
            skLineSegment(sketch, "E42.right", {"start": v(-0.75, 90.5) * mm, "end": v(-0.75, 78.5) * mm});
            skPoint(sketch, "E42.middle", {"position": v(0, 84.5) * mm});
            skLineSegment(sketch, "E43.1.0", {"start": v(-8.71, 90.08) * mm, "end": v(-10.2, 89.93) * mm});
            skLineSegment(sketch, "E43.1.1", {"start": v(-8.71, 90.08) * mm, "end": v(-7.46, 78.15) * mm});
            skLineSegment(sketch, "E43.1.2", {"start": v(-7.46, 78.15) * mm, "end": v(-8.95, 78) * mm});
            skLineSegment(sketch, "E43.1.3", {"start": v(-10.2, 89.93) * mm, "end": v(-8.95, 78) * mm});
            skLineSegment(sketch, "E43.2.0", {"start": v(-18.08, 88.68) * mm, "end": v(-19.55, 88.37) * mm});
            skLineSegment(sketch, "E43.2.1", {"start": v(-18.08, 88.68) * mm, "end": v(-15.59, 76.94) * mm});
            skLineSegment(sketch, "E43.2.2", {"start": v(-15.59, 76.94) * mm, "end": v(-17.05, 76.63) * mm});
            skLineSegment(sketch, "E43.2.3", {"start": v(-19.55, 88.37) * mm, "end": v(-17.05, 76.63) * mm});
            skPoint(sketch, "E43.center", {"position": v(0, 0) * mm});
            skLineSegment(sketch, "E44.2.3.0", {"start": v(-27.25, 86.3) * mm, "end": v(-28.68, 85.84) * mm});
            skLineSegment(sketch, "E44.3.3.0", {"start": v(-27.25, 86.3) * mm, "end": v(-23.54, 74.89) * mm});
            skLineSegment(sketch, "E44.6.3.0", {"start": v(-23.54, 74.89) * mm, "end": v(-24.97, 74.43) * mm});
            skLineSegment(sketch, "E44.9.3.0", {"start": v(-28.68, 85.84) * mm, "end": v(-24.97, 74.43) * mm});
            skLineSegment(sketch, "E44.2.4.0", {"start": v(-36.12, 82.98) * mm, "end": v(-37.5, 82.37) * mm});
            skLineSegment(sketch, "E44.3.4.0", {"start": v(-36.12, 82.98) * mm, "end": v(-31.24, 72.02) * mm});
            skLineSegment(sketch, "E44.6.4.0", {"start": v(-31.24, 72.02) * mm, "end": v(-32.61, 71.4) * mm});
            skLineSegment(sketch, "E44.9.4.0", {"start": v(-37.5, 82.37) * mm, "end": v(-32.61, 71.4) * mm});
            skLineSegment(sketch, "E44.2.5.0", {"start": v(-44.6, 78.75) * mm, "end": v(-45.9, 78) * mm});
            skLineSegment(sketch, "E44.3.5.0", {"start": v(-44.6, 78.75) * mm, "end": v(-38.6, 68.36) * mm});
            skLineSegment(sketch, "E44.6.5.0", {"start": v(-38.6, 68.36) * mm, "end": v(-39.9, 67.6) * mm});
            skLineSegment(sketch, "E44.9.5.0", {"start": v(-45.9, 78) * mm, "end": v(-39.9, 67.6) * mm});
            skLineSegment(sketch, "E44.2.6.0", {"start": v(-52.59, 73.66) * mm, "end": v(-53.8, 72.78) * mm});
            skLineSegment(sketch, "E44.3.6.0", {"start": v(-52.59, 73.66) * mm, "end": v(-45.53, 63.95) * mm});
            skLineSegment(sketch, "E44.6.6.0", {"start": v(-45.53, 63.95) * mm, "end": v(-46.75, 63.07) * mm});
            skLineSegment(sketch, "E44.9.6.0", {"start": v(-53.8, 72.78) * mm, "end": v(-46.75, 63.07) * mm});
            skLineSegment(sketch, "E44.2.7.0", {"start": v(-60, 67.76) * mm, "end": v(-61.11, 66.75) * mm});
            skLineSegment(sketch, "E44.3.7.0", {"start": v(-60, 67.76) * mm, "end": v(-51.97, 58.84) * mm});
            skLineSegment(sketch, "E44.6.7.0", {"start": v(-51.97, 58.84) * mm, "end": v(-53.08, 57.84) * mm});
            skLineSegment(sketch, "E44.9.7.0", {"start": v(-61.11, 66.75) * mm, "end": v(-53.08, 57.84) * mm});
            skLineSegment(sketch, "E44.2.8.0", {"start": v(-66.75, 61.11) * mm, "end": v(-67.76, 60) * mm});
            skLineSegment(sketch, "E44.3.8.0", {"start": v(-66.75, 61.11) * mm, "end": v(-57.84, 53.08) * mm});
            skLineSegment(sketch, "E44.6.8.0", {"start": v(-57.84, 53.08) * mm, "end": v(-58.84, 51.97) * mm});
            skLineSegment(sketch, "E44.9.8.0", {"start": v(-67.76, 60) * mm, "end": v(-58.84, 51.97) * mm});
            skLineSegment(sketch, "E44.2.9.0", {"start": v(-72.78, 53.8) * mm, "end": v(-73.66, 52.59) * mm});
            skLineSegment(sketch, "E44.3.9.0", {"start": v(-72.78, 53.8) * mm, "end": v(-63.07, 46.75) * mm});
            skLineSegment(sketch, "E44.6.9.0", {"start": v(-63.07, 46.75) * mm, "end": v(-63.95, 45.53) * mm});
            skLineSegment(sketch, "E44.9.9.0", {"start": v(-73.66, 52.59) * mm, "end": v(-63.95, 45.53) * mm});
            skLineSegment(sketch, "E44.2.10.0", {"start": v(-78, 45.9) * mm, "end": v(-78.75, 44.6) * mm});
            skLineSegment(sketch, "E44.3.10.0", {"start": v(-78, 45.9) * mm, "end": v(-67.6, 39.9) * mm});
            skLineSegment(sketch, "E44.6.10.0", {"start": v(-67.6, 39.9) * mm, "end": v(-68.36, 38.6) * mm});
            skLineSegment(sketch, "E44.9.10.0", {"start": v(-78.75, 44.6) * mm, "end": v(-68.36, 38.6) * mm});
            skLineSegment(sketch, "E44.2.11.0", {"start": v(-82.37, 37.5) * mm, "end": v(-82.98, 36.12) * mm});
            skLineSegment(sketch, "E44.3.11.0", {"start": v(-82.37, 37.5) * mm, "end": v(-71.4, 32.61) * mm});
            skLineSegment(sketch, "E44.6.11.0", {"start": v(-71.4, 32.61) * mm, "end": v(-72.02, 31.24) * mm});
            skLineSegment(sketch, "E44.9.11.0", {"start": v(-82.98, 36.12) * mm, "end": v(-72.02, 31.24) * mm});
            skLineSegment(sketch, "E44.2.12.0", {"start": v(-85.84, 28.68) * mm, "end": v(-86.3, 27.25) * mm});
            skLineSegment(sketch, "E44.3.12.0", {"start": v(-85.84, 28.68) * mm, "end": v(-74.43, 24.97) * mm});
            skLineSegment(sketch, "E44.6.12.0", {"start": v(-74.43, 24.97) * mm, "end": v(-74.89, 23.54) * mm});
            skLineSegment(sketch, "E44.9.12.0", {"start": v(-86.3, 27.25) * mm, "end": v(-74.89, 23.54) * mm});
            skLineSegment(sketch, "E44.2.13.0", {"start": v(-88.37, 19.55) * mm, "end": v(-88.68, 18.08) * mm});
            skLineSegment(sketch, "E44.3.13.0", {"start": v(-88.37, 19.55) * mm, "end": v(-76.63, 17.05) * mm});
            skLineSegment(sketch, "E44.6.13.0", {"start": v(-76.63, 17.05) * mm, "end": v(-76.94, 15.59) * mm});
            skLineSegment(sketch, "E44.9.13.0", {"start": v(-88.68, 18.08) * mm, "end": v(-76.94, 15.59) * mm});
            skLineSegment(sketch, "E44.2.14.0", {"start": v(-89.93, 10.2) * mm, "end": v(-90.08, 8.71) * mm});
            skLineSegment(sketch, "E44.3.14.0", {"start": v(-89.93, 10.2) * mm, "end": v(-78, 8.95) * mm});
            skLineSegment(sketch, "E44.6.14.0", {"start": v(-78, 8.95) * mm, "end": v(-78.15, 7.46) * mm});
            skLineSegment(sketch, "E44.9.14.0", {"start": v(-90.08, 8.71) * mm, "end": v(-78.15, 7.46) * mm});
            skLineSegment(sketch, "E44.2.15.0", {"start": v(-90.5, 0.75) * mm, "end": v(-90.5, -0.75) * mm});
            skLineSegment(sketch, "E44.3.15.0", {"start": v(-90.5, 0.75) * mm, "end": v(-78.5, 0.75) * mm});
            skLineSegment(sketch, "E44.6.15.0", {"start": v(-78.5, 0.75) * mm, "end": v(-78.5, -0.75) * mm});
            skLineSegment(sketch, "E44.9.15.0", {"start": v(-90.5, -0.75) * mm, "end": v(-78.5, -0.75) * mm});
            skLineSegment(sketch, "E44.2.16.0", {"start": v(-90.08, -8.71) * mm, "end": v(-89.93, -10.2) * mm});
            skLineSegment(sketch, "E44.3.16.0", {"start": v(-90.08, -8.71) * mm, "end": v(-78.15, -7.46) * mm});
            skLineSegment(sketch, "E44.6.16.0", {"start": v(-78.15, -7.46) * mm, "end": v(-78, -8.95) * mm});
            skLineSegment(sketch, "E44.9.16.0", {"start": v(-89.93, -10.2) * mm, "end": v(-78, -8.95) * mm});
            skLineSegment(sketch, "E44.2.17.0", {"start": v(-88.68, -18.08) * mm, "end": v(-88.37, -19.55) * mm});
            skLineSegment(sketch, "E44.3.17.0", {"start": v(-88.68, -18.08) * mm, "end": v(-76.94, -15.59) * mm});
            skLineSegment(sketch, "E44.6.17.0", {"start": v(-76.94, -15.59) * mm, "end": v(-76.63, -17.05) * mm});
            skLineSegment(sketch, "E44.9.17.0", {"start": v(-88.37, -19.55) * mm, "end": v(-76.63, -17.05) * mm});
            skLineSegment(sketch, "E44.2.18.0", {"start": v(-86.3, -27.25) * mm, "end": v(-85.84, -28.68) * mm});
            skLineSegment(sketch, "E44.3.18.0", {"start": v(-86.3, -27.25) * mm, "end": v(-74.89, -23.54) * mm});
            skLineSegment(sketch, "E44.6.18.0", {"start": v(-74.89, -23.54) * mm, "end": v(-74.43, -24.97) * mm});
            skLineSegment(sketch, "E44.9.18.0", {"start": v(-85.84, -28.68) * mm, "end": v(-74.43, -24.97) * mm});
            skLineSegment(sketch, "E44.2.19.0", {"start": v(-82.98, -36.12) * mm, "end": v(-82.37, -37.5) * mm});
            skLineSegment(sketch, "E44.3.19.0", {"start": v(-82.98, -36.12) * mm, "end": v(-72.02, -31.24) * mm});
            skLineSegment(sketch, "E44.6.19.0", {"start": v(-72.02, -31.24) * mm, "end": v(-71.4, -32.61) * mm});
            skLineSegment(sketch, "E44.9.19.0", {"start": v(-82.37, -37.5) * mm, "end": v(-71.4, -32.61) * mm});
            skLineSegment(sketch, "E44.2.20.0", {"start": v(-78.75, -44.6) * mm, "end": v(-78, -45.9) * mm});
            skLineSegment(sketch, "E44.3.20.0", {"start": v(-78.75, -44.6) * mm, "end": v(-68.36, -38.6) * mm});
            skLineSegment(sketch, "E44.6.20.0", {"start": v(-68.36, -38.6) * mm, "end": v(-67.6, -39.9) * mm});
            skLineSegment(sketch, "E44.9.20.0", {"start": v(-78, -45.9) * mm, "end": v(-67.6, -39.9) * mm});
            skLineSegment(sketch, "E44.2.21.0", {"start": v(-73.66, -52.59) * mm, "end": v(-72.78, -53.8) * mm});
            skLineSegment(sketch, "E44.3.21.0", {"start": v(-73.66, -52.59) * mm, "end": v(-63.95, -45.53) * mm});
            skLineSegment(sketch, "E44.6.21.0", {"start": v(-63.95, -45.53) * mm, "end": v(-63.07, -46.75) * mm});
            skLineSegment(sketch, "E44.9.21.0", {"start": v(-72.78, -53.8) * mm, "end": v(-63.07, -46.75) * mm});
            skLineSegment(sketch, "E44.2.22.0", {"start": v(-67.76, -60) * mm, "end": v(-66.75, -61.11) * mm});
            skLineSegment(sketch, "E44.3.22.0", {"start": v(-67.76, -60) * mm, "end": v(-58.84, -51.97) * mm});
            skLineSegment(sketch, "E44.6.22.0", {"start": v(-58.84, -51.97) * mm, "end": v(-57.84, -53.08) * mm});
            skLineSegment(sketch, "E44.9.22.0", {"start": v(-66.75, -61.11) * mm, "end": v(-57.84, -53.08) * mm});
            skLineSegment(sketch, "E44.2.23.0", {"start": v(-61.11, -66.75) * mm, "end": v(-60, -67.76) * mm});
            skLineSegment(sketch, "E44.3.23.0", {"start": v(-61.11, -66.75) * mm, "end": v(-53.08, -57.84) * mm});
            skLineSegment(sketch, "E44.6.23.0", {"start": v(-53.08, -57.84) * mm, "end": v(-51.97, -58.84) * mm});
            skLineSegment(sketch, "E44.9.23.0", {"start": v(-60, -67.76) * mm, "end": v(-51.97, -58.84) * mm});
            skLineSegment(sketch, "E44.2.24.0", {"start": v(-53.8, -72.78) * mm, "end": v(-52.59, -73.66) * mm});
            skLineSegment(sketch, "E44.3.24.0", {"start": v(-53.8, -72.78) * mm, "end": v(-46.75, -63.07) * mm});
            skLineSegment(sketch, "E44.6.24.0", {"start": v(-46.75, -63.07) * mm, "end": v(-45.53, -63.95) * mm});
            skLineSegment(sketch, "E44.9.24.0", {"start": v(-52.59, -73.66) * mm, "end": v(-45.53, -63.95) * mm});
            skLineSegment(sketch, "E44.2.25.0", {"start": v(-45.9, -78) * mm, "end": v(-44.6, -78.75) * mm});
            skLineSegment(sketch, "E44.3.25.0", {"start": v(-45.9, -78) * mm, "end": v(-39.9, -67.6) * mm});
            skLineSegment(sketch, "E44.6.25.0", {"start": v(-39.9, -67.6) * mm, "end": v(-38.6, -68.36) * mm});
            skLineSegment(sketch, "E44.9.25.0", {"start": v(-44.6, -78.75) * mm, "end": v(-38.6, -68.36) * mm});
            skLineSegment(sketch, "E44.2.26.0", {"start": v(-37.5, -82.37) * mm, "end": v(-36.12, -82.98) * mm});
            skLineSegment(sketch, "E44.3.26.0", {"start": v(-37.5, -82.37) * mm, "end": v(-32.61, -71.4) * mm});
            skLineSegment(sketch, "E44.6.26.0", {"start": v(-32.61, -71.4) * mm, "end": v(-31.24, -72.02) * mm});
            skLineSegment(sketch, "E44.9.26.0", {"start": v(-36.12, -82.98) * mm, "end": v(-31.24, -72.02) * mm});
            skLineSegment(sketch, "E44.2.27.0", {"start": v(-28.68, -85.84) * mm, "end": v(-27.25, -86.3) * mm});
            skLineSegment(sketch, "E44.3.27.0", {"start": v(-28.68, -85.84) * mm, "end": v(-24.97, -74.43) * mm});
            skLineSegment(sketch, "E44.6.27.0", {"start": v(-24.97, -74.43) * mm, "end": v(-23.54, -74.89) * mm});
            skLineSegment(sketch, "E44.9.27.0", {"start": v(-27.25, -86.3) * mm, "end": v(-23.54, -74.89) * mm});
            skLineSegment(sketch, "E44.2.28.0", {"start": v(-19.55, -88.37) * mm, "end": v(-18.08, -88.68) * mm});
            skLineSegment(sketch, "E44.3.28.0", {"start": v(-19.55, -88.37) * mm, "end": v(-17.05, -76.63) * mm});
            skLineSegment(sketch, "E44.6.28.0", {"start": v(-17.05, -76.63) * mm, "end": v(-15.59, -76.94) * mm});
            skLineSegment(sketch, "E44.9.28.0", {"start": v(-18.08, -88.68) * mm, "end": v(-15.59, -76.94) * mm});
            skLineSegment(sketch, "E44.2.29.0", {"start": v(-10.2, -89.93) * mm, "end": v(-8.71, -90.08) * mm});
            skLineSegment(sketch, "E44.3.29.0", {"start": v(-10.2, -89.93) * mm, "end": v(-8.95, -78) * mm});
            skLineSegment(sketch, "E44.6.29.0", {"start": v(-8.95, -78) * mm, "end": v(-7.46, -78.15) * mm});
            skLineSegment(sketch, "E44.9.29.0", {"start": v(-8.71, -90.08) * mm, "end": v(-7.46, -78.15) * mm});
            skLineSegment(sketch, "E44.2.30.0", {"start": v(-0.75, -90.5) * mm, "end": v(0.75, -90.5) * mm});
            skLineSegment(sketch, "E44.3.30.0", {"start": v(-0.75, -90.5) * mm, "end": v(-0.75, -78.5) * mm});
            skLineSegment(sketch, "E44.6.30.0", {"start": v(-0.75, -78.5) * mm, "end": v(0.75, -78.5) * mm});
            skLineSegment(sketch, "E44.9.30.0", {"start": v(0.75, -90.5) * mm, "end": v(0.75, -78.5) * mm});
            skLineSegment(sketch, "E44.2.31.0", {"start": v(8.71, -90.08) * mm, "end": v(10.2, -89.93) * mm});
            skLineSegment(sketch, "E44.3.31.0", {"start": v(8.71, -90.08) * mm, "end": v(7.46, -78.15) * mm});
            skLineSegment(sketch, "E44.6.31.0", {"start": v(7.46, -78.15) * mm, "end": v(8.95, -78) * mm});
            skLineSegment(sketch, "E44.9.31.0", {"start": v(10.2, -89.93) * mm, "end": v(8.95, -78) * mm});
            skLineSegment(sketch, "E44.2.32.0", {"start": v(18.08, -88.68) * mm, "end": v(19.55, -88.37) * mm});
            skLineSegment(sketch, "E44.3.32.0", {"start": v(18.08, -88.68) * mm, "end": v(15.59, -76.94) * mm});
            skLineSegment(sketch, "E44.6.32.0", {"start": v(15.59, -76.94) * mm, "end": v(17.05, -76.63) * mm});
            skLineSegment(sketch, "E44.9.32.0", {"start": v(19.55, -88.37) * mm, "end": v(17.05, -76.63) * mm});
            skLineSegment(sketch, "E44.2.33.0", {"start": v(27.25, -86.3) * mm, "end": v(28.68, -85.84) * mm});
            skLineSegment(sketch, "E44.3.33.0", {"start": v(27.25, -86.3) * mm, "end": v(23.54, -74.89) * mm});
            skLineSegment(sketch, "E44.6.33.0", {"start": v(23.54, -74.89) * mm, "end": v(24.97, -74.43) * mm});
            skLineSegment(sketch, "E44.9.33.0", {"start": v(28.68, -85.84) * mm, "end": v(24.97, -74.43) * mm});
            skLineSegment(sketch, "E44.2.34.0", {"start": v(36.12, -82.98) * mm, "end": v(37.5, -82.37) * mm});
            skLineSegment(sketch, "E44.3.34.0", {"start": v(36.12, -82.98) * mm, "end": v(31.24, -72.02) * mm});
            skLineSegment(sketch, "E44.6.34.0", {"start": v(31.24, -72.02) * mm, "end": v(32.61, -71.4) * mm});
            skLineSegment(sketch, "E44.9.34.0", {"start": v(37.5, -82.37) * mm, "end": v(32.61, -71.4) * mm});
            skLineSegment(sketch, "E44.2.35.0", {"start": v(44.6, -78.75) * mm, "end": v(45.9, -78) * mm});
            skLineSegment(sketch, "E44.3.35.0", {"start": v(44.6, -78.75) * mm, "end": v(38.6, -68.36) * mm});
            skLineSegment(sketch, "E44.6.35.0", {"start": v(38.6, -68.36) * mm, "end": v(39.9, -67.6) * mm});
            skLineSegment(sketch, "E44.9.35.0", {"start": v(45.9, -78) * mm, "end": v(39.9, -67.6) * mm});
            skLineSegment(sketch, "E44.2.36.0", {"start": v(52.59, -73.66) * mm, "end": v(53.8, -72.78) * mm});
            skLineSegment(sketch, "E44.3.36.0", {"start": v(52.59, -73.66) * mm, "end": v(45.53, -63.95) * mm});
            skLineSegment(sketch, "E44.6.36.0", {"start": v(45.53, -63.95) * mm, "end": v(46.75, -63.07) * mm});
            skLineSegment(sketch, "E44.9.36.0", {"start": v(53.8, -72.78) * mm, "end": v(46.75, -63.07) * mm});
            skLineSegment(sketch, "E44.2.37.0", {"start": v(60, -67.76) * mm, "end": v(61.11, -66.75) * mm});
            skLineSegment(sketch, "E44.3.37.0", {"start": v(60, -67.76) * mm, "end": v(51.97, -58.84) * mm});
            skLineSegment(sketch, "E44.6.37.0", {"start": v(51.97, -58.84) * mm, "end": v(53.08, -57.84) * mm});
            skLineSegment(sketch, "E44.9.37.0", {"start": v(61.11, -66.75) * mm, "end": v(53.08, -57.84) * mm});
            skLineSegment(sketch, "E44.2.38.0", {"start": v(66.75, -61.11) * mm, "end": v(67.76, -60) * mm});
            skLineSegment(sketch, "E44.3.38.0", {"start": v(66.75, -61.11) * mm, "end": v(57.84, -53.08) * mm});
            skLineSegment(sketch, "E44.6.38.0", {"start": v(57.84, -53.08) * mm, "end": v(58.84, -51.97) * mm});
            skLineSegment(sketch, "E44.9.38.0", {"start": v(67.76, -60) * mm, "end": v(58.84, -51.97) * mm});
            skLineSegment(sketch, "E44.2.39.0", {"start": v(72.78, -53.8) * mm, "end": v(73.66, -52.59) * mm});
            skLineSegment(sketch, "E44.3.39.0", {"start": v(72.78, -53.8) * mm, "end": v(63.07, -46.75) * mm});
            skLineSegment(sketch, "E44.6.39.0", {"start": v(63.07, -46.75) * mm, "end": v(63.95, -45.53) * mm});
            skLineSegment(sketch, "E44.9.39.0", {"start": v(73.66, -52.59) * mm, "end": v(63.95, -45.53) * mm});
            skLineSegment(sketch, "E44.2.40.0", {"start": v(78, -45.9) * mm, "end": v(78.75, -44.6) * mm});
            skLineSegment(sketch, "E44.3.40.0", {"start": v(78, -45.9) * mm, "end": v(67.6, -39.9) * mm});
            skLineSegment(sketch, "E44.6.40.0", {"start": v(67.6, -39.9) * mm, "end": v(68.36, -38.6) * mm});
            skLineSegment(sketch, "E44.9.40.0", {"start": v(78.75, -44.6) * mm, "end": v(68.36, -38.6) * mm});
            skLineSegment(sketch, "E44.2.41.0", {"start": v(82.37, -37.5) * mm, "end": v(82.98, -36.12) * mm});
            skLineSegment(sketch, "E44.3.41.0", {"start": v(82.37, -37.5) * mm, "end": v(71.4, -32.61) * mm});
            skLineSegment(sketch, "E44.6.41.0", {"start": v(71.4, -32.61) * mm, "end": v(72.02, -31.24) * mm});
            skLineSegment(sketch, "E44.9.41.0", {"start": v(82.98, -36.12) * mm, "end": v(72.02, -31.24) * mm});
            skLineSegment(sketch, "E44.2.42.0", {"start": v(85.84, -28.68) * mm, "end": v(86.3, -27.25) * mm});
            skLineSegment(sketch, "E44.3.42.0", {"start": v(85.84, -28.68) * mm, "end": v(74.43, -24.97) * mm});
            skLineSegment(sketch, "E44.6.42.0", {"start": v(74.43, -24.97) * mm, "end": v(74.89, -23.54) * mm});
            skLineSegment(sketch, "E44.9.42.0", {"start": v(86.3, -27.25) * mm, "end": v(74.89, -23.54) * mm});
            skLineSegment(sketch, "E44.2.43.0", {"start": v(88.37, -19.55) * mm, "end": v(88.68, -18.08) * mm});
            skLineSegment(sketch, "E44.3.43.0", {"start": v(88.37, -19.55) * mm, "end": v(76.63, -17.05) * mm});
            skLineSegment(sketch, "E44.6.43.0", {"start": v(76.63, -17.05) * mm, "end": v(76.94, -15.59) * mm});
            skLineSegment(sketch, "E44.9.43.0", {"start": v(88.68, -18.08) * mm, "end": v(76.94, -15.59) * mm});
            skLineSegment(sketch, "E44.2.44.0", {"start": v(89.93, -10.2) * mm, "end": v(90.08, -8.71) * mm});
            skLineSegment(sketch, "E44.3.44.0", {"start": v(89.93, -10.2) * mm, "end": v(78, -8.95) * mm});
            skLineSegment(sketch, "E44.6.44.0", {"start": v(78, -8.95) * mm, "end": v(78.15, -7.46) * mm});
            skLineSegment(sketch, "E44.9.44.0", {"start": v(90.08, -8.71) * mm, "end": v(78.15, -7.46) * mm});
            skLineSegment(sketch, "E44.2.45.0", {"start": v(90.5, -0.75) * mm, "end": v(90.5, 0.75) * mm});
            skLineSegment(sketch, "E44.3.45.0", {"start": v(90.5, -0.75) * mm, "end": v(78.5, -0.75) * mm});
            skLineSegment(sketch, "E44.6.45.0", {"start": v(78.5, -0.75) * mm, "end": v(78.5, 0.75) * mm});
            skLineSegment(sketch, "E44.9.45.0", {"start": v(90.5, 0.75) * mm, "end": v(78.5, 0.75) * mm});
            skLineSegment(sketch, "E44.2.46.0", {"start": v(90.08, 8.71) * mm, "end": v(89.93, 10.2) * mm});
            skLineSegment(sketch, "E44.3.46.0", {"start": v(90.08, 8.71) * mm, "end": v(78.15, 7.46) * mm});
            skLineSegment(sketch, "E44.6.46.0", {"start": v(78.15, 7.46) * mm, "end": v(78, 8.95) * mm});
            skLineSegment(sketch, "E44.9.46.0", {"start": v(89.93, 10.2) * mm, "end": v(78, 8.95) * mm});
            skLineSegment(sketch, "E44.2.47.0", {"start": v(88.68, 18.08) * mm, "end": v(88.37, 19.55) * mm});
            skLineSegment(sketch, "E44.3.47.0", {"start": v(88.68, 18.08) * mm, "end": v(76.94, 15.59) * mm});
            skLineSegment(sketch, "E44.6.47.0", {"start": v(76.94, 15.59) * mm, "end": v(76.63, 17.05) * mm});
            skLineSegment(sketch, "E44.9.47.0", {"start": v(88.37, 19.55) * mm, "end": v(76.63, 17.05) * mm});
            skLineSegment(sketch, "E44.2.48.0", {"start": v(86.3, 27.25) * mm, "end": v(85.84, 28.68) * mm});
            skLineSegment(sketch, "E44.3.48.0", {"start": v(86.3, 27.25) * mm, "end": v(74.89, 23.54) * mm});
            skLineSegment(sketch, "E44.6.48.0", {"start": v(74.89, 23.54) * mm, "end": v(74.43, 24.97) * mm});
            skLineSegment(sketch, "E44.9.48.0", {"start": v(85.84, 28.68) * mm, "end": v(74.43, 24.97) * mm});
            skLineSegment(sketch, "E44.2.49.0", {"start": v(82.98, 36.12) * mm, "end": v(82.37, 37.5) * mm});
            skLineSegment(sketch, "E44.3.49.0", {"start": v(82.98, 36.12) * mm, "end": v(72.02, 31.24) * mm});
            skLineSegment(sketch, "E44.6.49.0", {"start": v(72.02, 31.24) * mm, "end": v(71.4, 32.61) * mm});
            skLineSegment(sketch, "E44.9.49.0", {"start": v(82.37, 37.5) * mm, "end": v(71.4, 32.61) * mm});
            skLineSegment(sketch, "E44.2.50.0", {"start": v(78.75, 44.6) * mm, "end": v(78, 45.9) * mm});
            skLineSegment(sketch, "E44.3.50.0", {"start": v(78.75, 44.6) * mm, "end": v(68.36, 38.6) * mm});
            skLineSegment(sketch, "E44.6.50.0", {"start": v(68.36, 38.6) * mm, "end": v(67.6, 39.9) * mm});
            skLineSegment(sketch, "E44.9.50.0", {"start": v(78, 45.9) * mm, "end": v(67.6, 39.9) * mm});
            skLineSegment(sketch, "E44.2.51.0", {"start": v(73.66, 52.59) * mm, "end": v(72.78, 53.8) * mm});
            skLineSegment(sketch, "E44.3.51.0", {"start": v(73.66, 52.59) * mm, "end": v(63.95, 45.53) * mm});
            skLineSegment(sketch, "E44.6.51.0", {"start": v(63.95, 45.53) * mm, "end": v(63.07, 46.75) * mm});
            skLineSegment(sketch, "E44.9.51.0", {"start": v(72.78, 53.8) * mm, "end": v(63.07, 46.75) * mm});
            skLineSegment(sketch, "E44.2.52.0", {"start": v(67.76, 60) * mm, "end": v(66.75, 61.11) * mm});
            skLineSegment(sketch, "E44.3.52.0", {"start": v(67.76, 60) * mm, "end": v(58.84, 51.97) * mm});
            skLineSegment(sketch, "E44.6.52.0", {"start": v(58.84, 51.97) * mm, "end": v(57.84, 53.08) * mm});
            skLineSegment(sketch, "E44.9.52.0", {"start": v(66.75, 61.11) * mm, "end": v(57.84, 53.08) * mm});
            skLineSegment(sketch, "E44.2.53.0", {"start": v(61.11, 66.75) * mm, "end": v(60, 67.76) * mm});
            skLineSegment(sketch, "E44.3.53.0", {"start": v(61.11, 66.75) * mm, "end": v(53.08, 57.84) * mm});
            skLineSegment(sketch, "E44.6.53.0", {"start": v(53.08, 57.84) * mm, "end": v(51.97, 58.84) * mm});
            skLineSegment(sketch, "E44.9.53.0", {"start": v(60, 67.76) * mm, "end": v(51.97, 58.84) * mm});
            skLineSegment(sketch, "E44.2.54.0", {"start": v(53.8, 72.78) * mm, "end": v(52.59, 73.66) * mm});
            skLineSegment(sketch, "E44.3.54.0", {"start": v(53.8, 72.78) * mm, "end": v(46.75, 63.07) * mm});
            skLineSegment(sketch, "E44.6.54.0", {"start": v(46.75, 63.07) * mm, "end": v(45.53, 63.95) * mm});
            skLineSegment(sketch, "E44.9.54.0", {"start": v(52.59, 73.66) * mm, "end": v(45.53, 63.95) * mm});
            skLineSegment(sketch, "E44.2.55.0", {"start": v(45.9, 78) * mm, "end": v(44.6, 78.75) * mm});
            skLineSegment(sketch, "E44.3.55.0", {"start": v(45.9, 78) * mm, "end": v(39.9, 67.6) * mm});
            skLineSegment(sketch, "E44.6.55.0", {"start": v(39.9, 67.6) * mm, "end": v(38.6, 68.36) * mm});
            skLineSegment(sketch, "E44.9.55.0", {"start": v(44.6, 78.75) * mm, "end": v(38.6, 68.36) * mm});
            skLineSegment(sketch, "E44.2.56.0", {"start": v(37.5, 82.37) * mm, "end": v(36.12, 82.98) * mm});
            skLineSegment(sketch, "E44.3.56.0", {"start": v(37.5, 82.37) * mm, "end": v(32.61, 71.4) * mm});
            skLineSegment(sketch, "E44.6.56.0", {"start": v(32.61, 71.4) * mm, "end": v(31.24, 72.02) * mm});
            skLineSegment(sketch, "E44.9.56.0", {"start": v(36.12, 82.98) * mm, "end": v(31.24, 72.02) * mm});
            skLineSegment(sketch, "E44.2.57.0", {"start": v(28.68, 85.84) * mm, "end": v(27.25, 86.3) * mm});
            skLineSegment(sketch, "E44.3.57.0", {"start": v(28.68, 85.84) * mm, "end": v(24.97, 74.43) * mm});
            skLineSegment(sketch, "E44.6.57.0", {"start": v(24.97, 74.43) * mm, "end": v(23.54, 74.89) * mm});
            skLineSegment(sketch, "E44.9.57.0", {"start": v(27.25, 86.3) * mm, "end": v(23.54, 74.89) * mm});
            skLineSegment(sketch, "E44.2.58.0", {"start": v(19.55, 88.37) * mm, "end": v(18.08, 88.68) * mm});
            skLineSegment(sketch, "E44.3.58.0", {"start": v(19.55, 88.37) * mm, "end": v(17.05, 76.63) * mm});
            skLineSegment(sketch, "E44.6.58.0", {"start": v(17.05, 76.63) * mm, "end": v(15.59, 76.94) * mm});
            skLineSegment(sketch, "E44.9.58.0", {"start": v(18.08, 88.68) * mm, "end": v(15.59, 76.94) * mm});
            skLineSegment(sketch, "E44.2.59.0", {"start": v(10.2, 89.93) * mm, "end": v(8.71, 90.08) * mm});
            skLineSegment(sketch, "E44.3.59.0", {"start": v(10.2, 89.93) * mm, "end": v(8.95, 78) * mm});
            skLineSegment(sketch, "E44.6.59.0", {"start": v(8.95, 78) * mm, "end": v(7.46, 78.15) * mm});
            skLineSegment(sketch, "E44.9.59.0", {"start": v(8.71, 90.08) * mm, "end": v(7.46, 78.15) * mm});
            skSolve(sketch);
        }
        {
            var Q0;
            Q0 = qSketchRegion(id + "F27", true);
            extrude(context, id + "F28", {"entities" : qUnion([Q0]), "operationType" : NewBodyOperationType.REMOVE, "oppositeDirection" : true, "depth" : 0.2 * mm, "offsetDistance" : 25 * mm});
        }
        {
            var Q0;
            Q0=makeQuery(id+"F26.boolean.opBoolean","COPY",FACE,{"derivedFrom":makeQuery(id+"F26.opExtrude","CAP_FACE",FACE,{"disambiguationData":[OSD([sQuery(id+"F25.wireOp",EDGE,"E40.bottom"),sQuery(id+"F25.wireOp",EDGE,"E40.top"),sQuery(id+"F25.wireOp",EDGE,"E40.left"),sQuery(id+"F25.wireOp",EDGE,"E40.right")])],"isStart":false})});
            extrude(context, id + "F29", {"entities" : qUnion([Q0]), "depth" : 1 * mm, "offsetDistance" : 25 * mm});
        }
        {
            var Q0;
            Q0=makeQuery(id+"F28.boolean.opBoolean","COPY",FACE,{"derivedFrom":makeQuery(id+"F28.opExtrude","CAP_FACE",FACE,{"disambiguationData":[OSD([sQuery(id+"F27.wireOp",EDGE,"E44.2.59.0"),sQuery(id+"F27.wireOp",EDGE,"E44.3.59.0"),sQuery(id+"F27.wireOp",EDGE,"E44.6.59.0"),sQuery(id+"F27.wireOp",EDGE,"E44.9.59.0")])],"isStart":false})});
            extrude(context, id + "F30", {"entities" : qUnion([Q0]), "depth" : 0.4 * mm, "offsetDistance" : 25 * mm});
        }
    });
